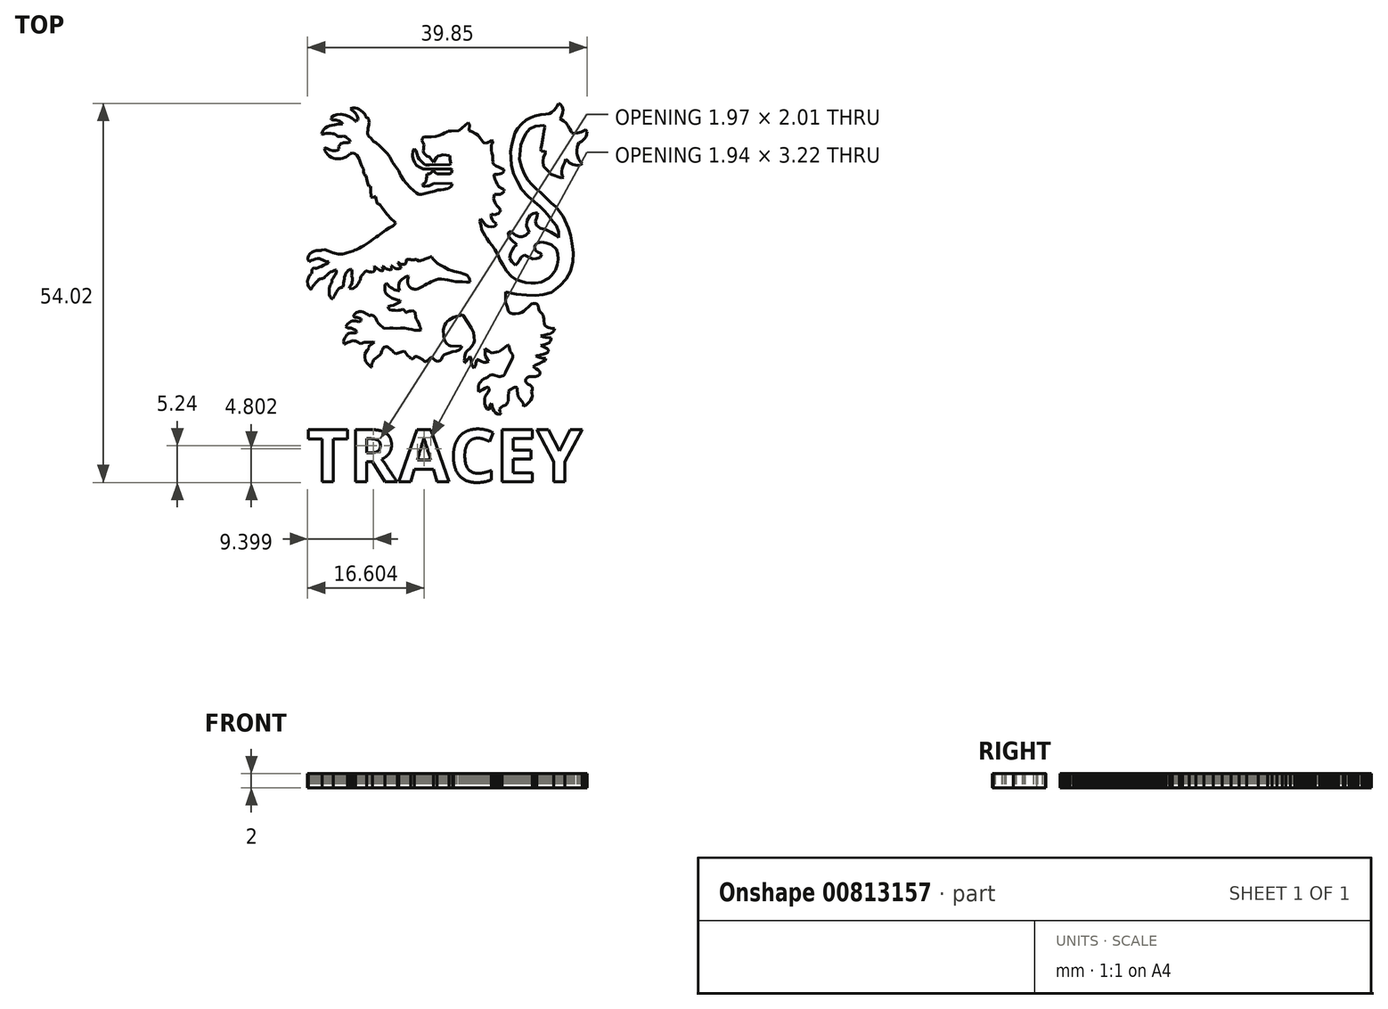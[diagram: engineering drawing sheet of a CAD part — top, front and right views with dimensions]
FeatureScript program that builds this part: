
annotation { "Feature Type Name" : "Feature", "Feature Type Description" : "" }
export const myFeature = defineFeature(function(context is Context, id is Id, definition is map)
    precondition{}
    {
        {
            var Q0;
            Q0=qCreatedBy(makeId("Top.planeOp"),FACE);
            var sketch = newSketch(context, id + "F0", { "sketchPlane" : qUnion([Q0])});
            skLineSegment(sketch, "E0", {"start": v(28.34, 17.71) * mm, "end": v(28.34, 16.2) * mm});
            skLineSegment(sketch, "E1", {"start": v(28.34, 16.2) * mm, "end": v(28.56, 15.55) * mm});
            skLineSegment(sketch, "E2", {"start": v(28.56, 15.55) * mm, "end": v(28.71, 15.03) * mm});
            skLineSegment(sketch, "E3", {"start": v(28.71, 15.03) * mm, "end": v(28.95, 14.75) * mm});
            skLineSegment(sketch, "E4", {"start": v(28.95, 14.75) * mm, "end": v(29.32, 14.64) * mm});
            skLineSegment(sketch, "E5", {"start": v(29.32, 14.64) * mm, "end": v(29.7, 14.64) * mm});
            skLineSegment(sketch, "E6", {"start": v(29.7, 14.64) * mm, "end": v(30.25, 14.7) * mm});
            skLineSegment(sketch, "E7", {"start": v(30.25, 14.7) * mm, "end": v(30.6, 14.84) * mm});
            skLineSegment(sketch, "E8", {"start": v(30.6, 14.84) * mm, "end": v(30.92, 15.03) * mm});
            skLineSegment(sketch, "E9", {"start": v(30.92, 15.03) * mm, "end": v(31.25, 15.3) * mm});
            skLineSegment(sketch, "E10", {"start": v(31.25, 15.3) * mm, "end": v(31.54, 15.57) * mm});
            skLineSegment(sketch, "E11", {"start": v(31.54, 15.57) * mm, "end": v(31.8, 15.85) * mm});
            skLineSegment(sketch, "E12", {"start": v(31.8, 15.85) * mm, "end": v(32.02, 16.03) * mm});
            skLineSegment(sketch, "E13", {"start": v(32.02, 16.03) * mm, "end": v(32.3, 16.1) * mm});
            skLineSegment(sketch, "E14", {"start": v(32.3, 16.1) * mm, "end": v(32.6, 16.1) * mm});
            skLineSegment(sketch, "E15", {"start": v(32.6, 16.1) * mm, "end": v(32.8, 16.04) * mm});
            skLineSegment(sketch, "E16", {"start": v(32.8, 16.04) * mm, "end": v(32.94, 15.82) * mm});
            skLineSegment(sketch, "E17", {"start": v(32.94, 15.82) * mm, "end": v(33.05, 15.36) * mm});
            skLineSegment(sketch, "E18", {"start": v(33.05, 15.36) * mm, "end": v(33.13, 15.03) * mm});
            skLineSegment(sketch, "E19", {"start": v(33.13, 15.03) * mm, "end": v(33.33, 14.83) * mm});
            skLineSegment(sketch, "E20", {"start": v(33.33, 14.83) * mm, "end": v(33.51, 14.64) * mm});
            skLineSegment(sketch, "E21", {"start": v(33.51, 14.64) * mm, "end": v(33.65, 14.4) * mm});
            skLineSegment(sketch, "E22", {"start": v(33.65, 14.4) * mm, "end": v(33.71, 14.17) * mm});
            skLineSegment(sketch, "E23", {"start": v(33.71, 14.17) * mm, "end": v(33.76, 13.87) * mm});
            skLineSegment(sketch, "E24", {"start": v(33.76, 13.87) * mm, "end": v(33.76, 13.58) * mm});
            skLineSegment(sketch, "E25", {"start": v(33.76, 13.58) * mm, "end": v(33.83, 13.25) * mm});
            skLineSegment(sketch, "E26", {"start": v(33.83, 13.25) * mm, "end": v(33.93, 12.98) * mm});
            skLineSegment(sketch, "E27", {"start": v(33.93, 12.98) * mm, "end": v(34.15, 12.8) * mm});
            skLineSegment(sketch, "E28", {"start": v(34.15, 12.8) * mm, "end": v(34.43, 12.66) * mm});
            skLineSegment(sketch, "E29", {"start": v(34.43, 12.66) * mm, "end": v(34.7, 12.58) * mm});
            skLineSegment(sketch, "E30", {"start": v(34.7, 12.58) * mm, "end": v(34.98, 12.5) * mm});
            skLineSegment(sketch, "E31", {"start": v(34.98, 12.5) * mm, "end": v(35.33, 12.5) * mm});
            skLineSegment(sketch, "E32", {"start": v(35.33, 12.5) * mm, "end": v(35.27, 12.3) * mm});
            skLineSegment(sketch, "E33", {"start": v(35.27, 12.3) * mm, "end": v(35.09, 12) * mm});
            skLineSegment(sketch, "E34", {"start": v(35.09, 12) * mm, "end": v(34.7, 11.8) * mm});
            skLineSegment(sketch, "E35", {"start": v(34.7, 11.8) * mm, "end": v(34.29, 11.7) * mm});
            skPoint(sketch, "E35.endSnap0", {"position": v(34.29, 12.73) * mm});
            skLineSegment(sketch, "E36", {"start": v(34.29, 11.7) * mm, "end": v(33.84, 11.57) * mm});
            skLineSegment(sketch, "E37", {"start": v(33.84, 11.57) * mm, "end": v(33.46, 11.52) * mm});
            skLineSegment(sketch, "E38", {"start": v(33.46, 11.52) * mm, "end": v(33.33, 11.44) * mm});
            skLineSegment(sketch, "E39", {"start": v(33.33, 11.44) * mm, "end": v(33.73, 11.33) * mm});
            skLineSegment(sketch, "E40", {"start": v(33.73, 11.33) * mm, "end": v(34.07, 11.28) * mm});
            skLineSegment(sketch, "E41", {"start": v(34.07, 11.28) * mm, "end": v(34.56, 11.22) * mm});
            skLineSegment(sketch, "E42", {"start": v(34.56, 11.22) * mm, "end": v(34.78, 11.22) * mm});
            skLineSegment(sketch, "E43", {"start": v(34.78, 11.22) * mm, "end": v(34.81, 10.91) * mm});
            skLineSegment(sketch, "E44", {"start": v(34.81, 10.91) * mm, "end": v(34.7, 10.7) * mm});
            skLineSegment(sketch, "E45", {"start": v(34.7, 10.7) * mm, "end": v(34.52, 10.52) * mm});
            skLineSegment(sketch, "E46", {"start": v(34.52, 10.52) * mm, "end": v(34.22, 10.35) * mm});
            skLineSegment(sketch, "E47", {"start": v(34.22, 10.35) * mm, "end": v(33.93, 10.26) * mm});
            skLineSegment(sketch, "E48", {"start": v(33.93, 10.26) * mm, "end": v(33.64, 10.19) * mm});
            skLineSegment(sketch, "E49", {"start": v(33.64, 10.19) * mm, "end": v(33.35, 10.14) * mm});
            skLineSegment(sketch, "E50", {"start": v(33.35, 10.14) * mm, "end": v(33.36, 10.09) * mm});
            skLineSegment(sketch, "E51", {"start": v(33.36, 10.09) * mm, "end": v(33.72, 9.9) * mm});
            skLineSegment(sketch, "E52", {"start": v(33.72, 9.9) * mm, "end": v(33.99, 9.77) * mm});
            skLineSegment(sketch, "E53", {"start": v(33.99, 9.77) * mm, "end": v(34.23, 9.64) * mm});
            skLineSegment(sketch, "E54", {"start": v(34.23, 9.64) * mm, "end": v(34.43, 9.48) * mm});
            skLineSegment(sketch, "E55", {"start": v(34.43, 9.48) * mm, "end": v(34.43, 9.29) * mm});
            skLineSegment(sketch, "E56", {"start": v(34.43, 9.29) * mm, "end": v(34.3, 9.12) * mm});
            skLineSegment(sketch, "E57", {"start": v(34.3, 9.12) * mm, "end": v(34.01, 8.96) * mm});
            skLineSegment(sketch, "E58", {"start": v(34.01, 8.96) * mm, "end": v(33.68, 8.84) * mm});
            skLineSegment(sketch, "E59", {"start": v(33.68, 8.84) * mm, "end": v(33.36, 8.75) * mm});
            skLineSegment(sketch, "E60", {"start": v(33.36, 8.75) * mm, "end": v(33.04, 8.68) * mm});
            skLineSegment(sketch, "E61", {"start": v(33.04, 8.68) * mm, "end": v(32.74, 8.62) * mm});
            skLineSegment(sketch, "E62", {"start": v(32.74, 8.62) * mm, "end": v(32.64, 8.59) * mm});
            skLineSegment(sketch, "E63", {"start": v(32.64, 8.59) * mm, "end": v(32.97, 8.49) * mm});
            skLineSegment(sketch, "E64", {"start": v(32.97, 8.49) * mm, "end": v(33.15, 8.4) * mm});
            skLineSegment(sketch, "E65", {"start": v(33.15, 8.4) * mm, "end": v(33.42, 8.31) * mm});
            skLineSegment(sketch, "E66", {"start": v(33.42, 8.31) * mm, "end": v(33.66, 8.29) * mm});
            skLineSegment(sketch, "E67", {"start": v(33.66, 8.29) * mm, "end": v(33.93, 8.29) * mm});
            skLineSegment(sketch, "E68", {"start": v(33.93, 8.29) * mm, "end": v(34.01, 8.26) * mm});
            skLineSegment(sketch, "E69", {"start": v(34.01, 8.26) * mm, "end": v(33.99, 7.95) * mm});
            skLineSegment(sketch, "E70", {"start": v(33.99, 7.95) * mm, "end": v(33.56, 7.73) * mm});
            skLineSegment(sketch, "E71", {"start": v(33.56, 7.73) * mm, "end": v(33.11, 7.52) * mm});
            skLineSegment(sketch, "E72", {"start": v(33.11, 7.52) * mm, "end": v(32.6, 7.32) * mm});
            skLineSegment(sketch, "E73", {"start": v(32.6, 7.32) * mm, "end": v(32.31, 7.16) * mm});
            skLineSegment(sketch, "E74", {"start": v(32.31, 7.16) * mm, "end": v(32.24, 7.09) * mm});
            skLineSegment(sketch, "E75", {"start": v(32.24, 7.09) * mm, "end": v(32.66, 6.84) * mm});
            skLineSegment(sketch, "E76", {"start": v(32.66, 6.84) * mm, "end": v(32.94, 6.63) * mm});
            skLineSegment(sketch, "E77", {"start": v(32.94, 6.63) * mm, "end": v(33.14, 6.43) * mm});
            skLineSegment(sketch, "E78", {"start": v(33.14, 6.43) * mm, "end": v(33.23, 6.27) * mm});
            skLineSegment(sketch, "E79", {"start": v(33.23, 6.27) * mm, "end": v(33.23, 5.99) * mm});
            skLineSegment(sketch, "E80", {"start": v(33.23, 5.99) * mm, "end": v(32.97, 5.78) * mm});
            skLineSegment(sketch, "E81", {"start": v(32.97, 5.78) * mm, "end": v(32.6, 5.7) * mm});
            skLineSegment(sketch, "E82", {"start": v(32.6, 5.7) * mm, "end": v(32.13, 5.7) * mm});
            skLineSegment(sketch, "E83", {"start": v(32.13, 5.7) * mm, "end": v(31.71, 5.7) * mm});
            skLineSegment(sketch, "E84", {"start": v(31.71, 5.7) * mm, "end": v(31.42, 5.56) * mm});
            skLineSegment(sketch, "E85", {"start": v(31.42, 5.56) * mm, "end": v(31.25, 5.36) * mm});
            skLineSegment(sketch, "E86", {"start": v(31.25, 5.36) * mm, "end": v(31.2, 5.21) * mm});
            skLineSegment(sketch, "E87", {"start": v(31.2, 5.21) * mm, "end": v(31.2, 5.07) * mm});
            skLineSegment(sketch, "E88", {"start": v(31.2, 5.07) * mm, "end": v(31.22, 4.95) * mm});
            skLineSegment(sketch, "E89", {"start": v(31.22, 4.95) * mm, "end": v(31.27, 4.82) * mm});
            skLineSegment(sketch, "E90", {"start": v(31.27, 4.82) * mm, "end": v(31.37, 4.69) * mm});
            skLineSegment(sketch, "E91", {"start": v(31.37, 4.69) * mm, "end": v(31.5, 4.61) * mm});
            skLineSegment(sketch, "E92", {"start": v(31.5, 4.61) * mm, "end": v(31.63, 4.52) * mm});
            skLineSegment(sketch, "E93", {"start": v(31.63, 4.52) * mm, "end": v(31.8, 4.44) * mm});
            skLineSegment(sketch, "E94", {"start": v(31.8, 4.44) * mm, "end": v(31.95, 4.33) * mm});
            skLineSegment(sketch, "E95", {"start": v(31.95, 4.33) * mm, "end": v(32.08, 4.2) * mm});
            skLineSegment(sketch, "E96", {"start": v(32.08, 4.2) * mm, "end": v(32.15, 4.06) * mm});
            skLineSegment(sketch, "E97", {"start": v(32.15, 4.06) * mm, "end": v(32.13, 3.81) * mm});
            skLineSegment(sketch, "E98", {"start": v(32.13, 3.81) * mm, "end": v(32.05, 3.64) * mm});
            skLineSegment(sketch, "E99", {"start": v(32.05, 3.64) * mm, "end": v(31.98, 3.52) * mm});
            skLineSegment(sketch, "E100", {"start": v(31.98, 3.52) * mm, "end": v(32.06, 3.31) * mm});
            skLineSegment(sketch, "E101", {"start": v(32.06, 3.31) * mm, "end": v(32.1, 3.15) * mm});
            skLineSegment(sketch, "E102", {"start": v(32.1, 3.15) * mm, "end": v(32.15, 2.91) * mm});
            skLineSegment(sketch, "E103", {"start": v(32.15, 2.91) * mm, "end": v(32.05, 2.6) * mm});
            skLineSegment(sketch, "E104", {"start": v(32.05, 2.6) * mm, "end": v(31.9, 2.32) * mm});
            skLineSegment(sketch, "E105", {"start": v(31.9, 2.32) * mm, "end": v(31.75, 2.1) * mm});
            skLineSegment(sketch, "E106", {"start": v(31.75, 2.1) * mm, "end": v(31.46, 1.82) * mm});
            skLineSegment(sketch, "E107", {"start": v(31.46, 1.82) * mm, "end": v(31.25, 1.61) * mm});
            skLineSegment(sketch, "E108", {"start": v(31.25, 1.61) * mm, "end": v(30.95, 1.48) * mm});
            skLineSegment(sketch, "E109", {"start": v(30.95, 1.48) * mm, "end": v(30.85, 1.43) * mm});
            skLineSegment(sketch, "E110", {"start": v(30.85, 1.43) * mm, "end": v(30.9, 1.83) * mm});
            skLineSegment(sketch, "E111", {"start": v(30.9, 1.83) * mm, "end": v(30.64, 2.2) * mm});
            skLineSegment(sketch, "E112", {"start": v(30.64, 2.2) * mm, "end": v(30.14, 2.84) * mm});
            skLineSegment(sketch, "E113", {"start": v(30.14, 2.84) * mm, "end": v(30.04, 3.24) * mm});
            skLineSegment(sketch, "E114", {"start": v(30.04, 3.24) * mm, "end": v(29.97, 3.72) * mm});
            skLineSegment(sketch, "E115", {"start": v(29.97, 3.72) * mm, "end": v(29.97, 4.06) * mm});
            skLineSegment(sketch, "E116", {"start": v(29.97, 4.06) * mm, "end": v(29.84, 4.15) * mm});
            skLineSegment(sketch, "E117", {"start": v(29.84, 4.15) * mm, "end": v(29.57, 4.11) * mm});
            skLineSegment(sketch, "E118", {"start": v(29.57, 4.11) * mm, "end": v(29.25, 3.93) * mm});
            skLineSegment(sketch, "E119", {"start": v(29.25, 3.93) * mm, "end": v(28.9, 3.74) * mm});
            skLineSegment(sketch, "E120", {"start": v(28.9, 3.74) * mm, "end": v(28.71, 3.56) * mm});
            skLineSegment(sketch, "E121", {"start": v(28.71, 3.56) * mm, "end": v(28.74, 3.42) * mm});
            skLineSegment(sketch, "E122", {"start": v(28.74, 3.42) * mm, "end": v(28.71, 2.94) * mm});
            skLineSegment(sketch, "E123", {"start": v(28.71, 2.94) * mm, "end": v(28.71, 2.18) * mm});
            skLineSegment(sketch, "E124", {"start": v(28.71, 2.18) * mm, "end": v(28.6, 1.96) * mm});
            skLineSegment(sketch, "E125", {"start": v(28.6, 1.96) * mm, "end": v(28.55, 1.77) * mm});
            skLineSegment(sketch, "E126", {"start": v(28.55, 1.77) * mm, "end": v(28.34, 1.58) * mm});
            skLineSegment(sketch, "E127", {"start": v(28.34, 1.58) * mm, "end": v(27.92, 1.48) * mm});
            skLineSegment(sketch, "E128", {"start": v(27.92, 1.48) * mm, "end": v(27.7, 1.3) * mm});
            skLineSegment(sketch, "E129", {"start": v(27.7, 1.3) * mm, "end": v(27.45, 1.02) * mm});
            skLineSegment(sketch, "E130", {"start": v(27.45, 1.02) * mm, "end": v(27.51, 0.72) * mm});
            skLineSegment(sketch, "E131", {"start": v(27.51, 0.72) * mm, "end": v(27.62, 0.54) * mm});
            skLineSegment(sketch, "E132", {"start": v(27.62, 0.54) * mm, "end": v(27.56, 0.35) * mm});
            skLineSegment(sketch, "E133", {"start": v(27.56, 0.35) * mm, "end": v(27.35, 0.24) * mm});
            skLineSegment(sketch, "E134", {"start": v(27.35, 0.24) * mm, "end": v(27.18, 0.32) * mm});
            skLineSegment(sketch, "E135", {"start": v(27.18, 0.32) * mm, "end": v(26.9, 0.53) * mm});
            skLineSegment(sketch, "E136", {"start": v(26.9, 0.53) * mm, "end": v(26.68, 0.8) * mm});
            skLineSegment(sketch, "E137", {"start": v(26.68, 0.8) * mm, "end": v(26.47, 1.12) * mm});
            skLineSegment(sketch, "E138", {"start": v(26.47, 1.12) * mm, "end": v(26.41, 1.5) * mm});
            skLineSegment(sketch, "E139", {"start": v(26.41, 1.5) * mm, "end": v(26.37, 1.76) * mm});
            skLineSegment(sketch, "E140", {"start": v(26.37, 1.76) * mm, "end": v(26.32, 1.84) * mm});
            skLineSegment(sketch, "E141", {"start": v(26.32, 1.84) * mm, "end": v(26.2, 1.7) * mm});
            skLineSegment(sketch, "E142", {"start": v(26.2, 1.7) * mm, "end": v(26.12, 1.47) * mm});
            skLineSegment(sketch, "E143", {"start": v(26.12, 1.47) * mm, "end": v(26.07, 1.3) * mm});
            skLineSegment(sketch, "E144", {"start": v(26.07, 1.3) * mm, "end": v(26.07, 1.14) * mm});
            skLineSegment(sketch, "E145", {"start": v(26.07, 1.14) * mm, "end": v(26.07, 0.96) * mm});
            skLineSegment(sketch, "E146", {"start": v(26.07, 0.96) * mm, "end": v(25.73, 1.02) * mm});
            skLineSegment(sketch, "E147", {"start": v(25.73, 1.02) * mm, "end": v(25.4, 1.53) * mm});
            skLineSegment(sketch, "E148", {"start": v(25.4, 1.53) * mm, "end": v(25.32, 1.85) * mm});
            skLineSegment(sketch, "E149", {"start": v(25.32, 1.85) * mm, "end": v(25.32, 2.5) * mm});
            skLineSegment(sketch, "E150", {"start": v(25.32, 2.5) * mm, "end": v(25.43, 2.86) * mm});
            skLineSegment(sketch, "E151", {"start": v(25.43, 2.86) * mm, "end": v(25.64, 3.16) * mm});
            skLineSegment(sketch, "E152", {"start": v(25.64, 3.16) * mm, "end": v(25.85, 3.44) * mm});
            skLineSegment(sketch, "E153", {"start": v(25.85, 3.44) * mm, "end": v(26, 3.74) * mm});
            skLineSegment(sketch, "E154", {"start": v(26, 3.74) * mm, "end": v(26, 3.97) * mm});
            skLineSegment(sketch, "E155", {"start": v(26, 3.97) * mm, "end": v(25.84, 4.11) * mm});
            skLineSegment(sketch, "E156", {"start": v(25.84, 4.11) * mm, "end": v(25.68, 4.11) * mm});
            skLineSegment(sketch, "E157", {"start": v(25.68, 4.11) * mm, "end": v(25.43, 4.02) * mm});
            skLineSegment(sketch, "E158", {"start": v(25.43, 4.02) * mm, "end": v(25.09, 3.83) * mm});
            skLineSegment(sketch, "E159", {"start": v(25.09, 3.83) * mm, "end": v(24.86, 3.68) * mm});
            skLineSegment(sketch, "E160", {"start": v(24.86, 3.68) * mm, "end": v(24.55, 3.48) * mm});
            skLineSegment(sketch, "E161", {"start": v(24.55, 3.48) * mm, "end": v(24.48, 3.69) * mm});
            skLineSegment(sketch, "E162", {"start": v(24.48, 3.69) * mm, "end": v(24.48, 3.93) * mm});
            skLineSegment(sketch, "E163", {"start": v(24.48, 3.93) * mm, "end": v(24.48, 4.23) * mm});
            skLineSegment(sketch, "E164", {"start": v(24.48, 4.23) * mm, "end": v(24.55, 4.66) * mm});
            skLineSegment(sketch, "E165", {"start": v(24.55, 4.66) * mm, "end": v(24.74, 4.93) * mm});
            skLineSegment(sketch, "E166", {"start": v(24.74, 4.93) * mm, "end": v(24.96, 5.17) * mm});
            skLineSegment(sketch, "E167", {"start": v(24.96, 5.17) * mm, "end": v(25.24, 5.32) * mm});
            skLineSegment(sketch, "E168", {"start": v(25.24, 5.32) * mm, "end": v(25.55, 5.45) * mm});
            skLineSegment(sketch, "E169", {"start": v(25.55, 5.45) * mm, "end": v(25.69, 5.48) * mm});
            skLineSegment(sketch, "E170", {"start": v(25.69, 5.48) * mm, "end": v(25.91, 5.73) * mm});
            skLineSegment(sketch, "E171", {"start": v(25.91, 5.73) * mm, "end": v(26.12, 5.85) * mm});
            skLineSegment(sketch, "E172", {"start": v(26.12, 5.85) * mm, "end": v(26.35, 5.93) * mm});
            skLineSegment(sketch, "E173", {"start": v(26.35, 5.93) * mm, "end": v(26.54, 5.93) * mm});
            skLineSegment(sketch, "E174", {"start": v(26.54, 5.93) * mm, "end": v(26.78, 5.86) * mm});
            skLineSegment(sketch, "E175", {"start": v(26.78, 5.86) * mm, "end": v(27, 5.8) * mm});
            skLineSegment(sketch, "E176", {"start": v(27, 5.8) * mm, "end": v(27.15, 5.75) * mm});
            skLineSegment(sketch, "E177", {"start": v(27.15, 5.75) * mm, "end": v(27.38, 5.68) * mm});
            skLineSegment(sketch, "E178", {"start": v(27.38, 5.68) * mm, "end": v(27.58, 5.68) * mm});
            skLineSegment(sketch, "E179", {"start": v(27.58, 5.68) * mm, "end": v(27.78, 5.72) * mm});
            skLineSegment(sketch, "E180", {"start": v(27.78, 5.72) * mm, "end": v(28, 5.8) * mm});
            skLineSegment(sketch, "E181", {"start": v(28, 5.8) * mm, "end": v(28.13, 5.92) * mm});
            skLineSegment(sketch, "E182", {"start": v(28.13, 5.92) * mm, "end": v(28.27, 6.12) * mm});
            skLineSegment(sketch, "E183", {"start": v(28.27, 6.12) * mm, "end": v(28.34, 6.35) * mm});
            skLineSegment(sketch, "E184", {"start": v(28.34, 6.35) * mm, "end": v(29.3, 8.22) * mm});
            skLineSegment(sketch, "E185", {"start": v(29.3, 8.22) * mm, "end": v(29.36, 8.45) * mm});
            skLineSegment(sketch, "E186", {"start": v(29.36, 8.45) * mm, "end": v(29.32, 8.78) * mm});
            skLineSegment(sketch, "E187", {"start": v(29.32, 8.78) * mm, "end": v(29.1, 9.12) * mm});
            skLineSegment(sketch, "E188", {"start": v(29.1, 9.12) * mm, "end": v(28.97, 9.32) * mm});
            skLineSegment(sketch, "E189", {"start": v(28.97, 9.32) * mm, "end": v(28.9, 9.66) * mm});
            skLineSegment(sketch, "E190", {"start": v(28.9, 9.66) * mm, "end": v(28.82, 9.97) * mm});
            skLineSegment(sketch, "E191", {"start": v(28.82, 9.97) * mm, "end": v(28.78, 10.13) * mm});
            skLineSegment(sketch, "E192", {"start": v(28.78, 10.13) * mm, "end": v(28.67, 10.16) * mm});
            skLineSegment(sketch, "E193", {"start": v(28.67, 10.16) * mm, "end": v(28.53, 10.05) * mm});
            skLineSegment(sketch, "E194", {"start": v(28.53, 10.05) * mm, "end": v(28.24, 9.82) * mm});
            skLineSegment(sketch, "E195", {"start": v(28.24, 9.82) * mm, "end": v(28.04, 9.66) * mm});
            skLineSegment(sketch, "E196", {"start": v(28.04, 9.66) * mm, "end": v(27.74, 9.46) * mm});
            skLineSegment(sketch, "E197", {"start": v(27.74, 9.46) * mm, "end": v(27.35, 9.25) * mm});
            skLineSegment(sketch, "E198", {"start": v(27.35, 9.25) * mm, "end": v(27, 9.14) * mm});
            skLineSegment(sketch, "E199", {"start": v(27, 9.14) * mm, "end": v(26.37, 9.05) * mm});
            skLineSegment(sketch, "E200", {"start": v(26.37, 9.05) * mm, "end": v(25.9, 9.29) * mm});
            skLineSegment(sketch, "E201", {"start": v(25.9, 9.29) * mm, "end": v(25.43, 9.63) * mm});
            skLineSegment(sketch, "E202", {"start": v(25.43, 9.63) * mm, "end": v(25.34, 9.66) * mm});
            skLineSegment(sketch, "E203", {"start": v(25.34, 9.66) * mm, "end": v(25.4, 9.42) * mm});
            skLineSegment(sketch, "E204", {"start": v(25.4, 9.42) * mm, "end": v(25.4, 9.12) * mm});
            skLineSegment(sketch, "E205", {"start": v(25.4, 9.12) * mm, "end": v(25.43, 8.86) * mm});
            skLineSegment(sketch, "E206", {"start": v(25.43, 8.86) * mm, "end": v(25.5, 8.54) * mm});
            skLineSegment(sketch, "E207", {"start": v(25.5, 8.54) * mm, "end": v(25.7, 8.2) * mm});
            skLineSegment(sketch, "E208", {"start": v(25.7, 8.2) * mm, "end": v(25.9, 7.85) * mm});
            skLineSegment(sketch, "E209", {"start": v(25.9, 7.85) * mm, "end": v(25.55, 7.7) * mm});
            skLineSegment(sketch, "E210", {"start": v(25.55, 7.7) * mm, "end": v(25.24, 7.7) * mm});
            skLineSegment(sketch, "E211", {"start": v(25.24, 7.7) * mm, "end": v(24.92, 7.8) * mm});
            skLineSegment(sketch, "E212", {"start": v(24.92, 7.8) * mm, "end": v(24.57, 7.98) * mm});
            skLineSegment(sketch, "E213", {"start": v(24.57, 7.98) * mm, "end": v(24.37, 8.08) * mm});
            skLineSegment(sketch, "E214", {"start": v(24.37, 8.08) * mm, "end": v(24.2, 8.08) * mm});
            skLineSegment(sketch, "E215", {"start": v(24.2, 8.08) * mm, "end": v(24.2, 7.96) * mm});
            skLineSegment(sketch, "E216", {"start": v(24.2, 7.96) * mm, "end": v(24.12, 7.73) * mm});
            skLineSegment(sketch, "E217", {"start": v(24.12, 7.73) * mm, "end": v(24.07, 7.57) * mm});
            skLineSegment(sketch, "E218", {"start": v(24.07, 7.57) * mm, "end": v(24.05, 7.4) * mm});
            skLineSegment(sketch, "E219", {"start": v(24.05, 7.4) * mm, "end": v(24, 7.23) * mm});
            skLineSegment(sketch, "E220", {"start": v(24, 7.23) * mm, "end": v(23.96, 7.1) * mm});
            skLineSegment(sketch, "E221", {"start": v(23.96, 7.1) * mm, "end": v(23.84, 6.85) * mm});
            skLineSegment(sketch, "E222", {"start": v(23.84, 6.85) * mm, "end": v(23.57, 7.2) * mm});
            skLineSegment(sketch, "E223", {"start": v(23.57, 7.2) * mm, "end": v(23.46, 7.65) * mm});
            skLineSegment(sketch, "E224", {"start": v(23.46, 7.65) * mm, "end": v(23.39, 8.17) * mm});
            skLineSegment(sketch, "E225", {"start": v(23.39, 8.17) * mm, "end": v(23.31, 8.49) * mm});
            skLineSegment(sketch, "E226", {"start": v(23.31, 8.49) * mm, "end": v(23.22, 8.55) * mm});
            skLineSegment(sketch, "E227", {"start": v(23.22, 8.55) * mm, "end": v(23.17, 8.48) * mm});
            skLineSegment(sketch, "E228", {"start": v(23.17, 8.48) * mm, "end": v(23.05, 8.24) * mm});
            skLineSegment(sketch, "E229", {"start": v(23.05, 8.24) * mm, "end": v(22.87, 8.03) * mm});
            skLineSegment(sketch, "E230", {"start": v(22.87, 8.03) * mm, "end": v(22.7, 7.85) * mm});
            skLineSegment(sketch, "E231", {"start": v(22.7, 7.85) * mm, "end": v(22.58, 7.68) * mm});
            skLineSegment(sketch, "E232", {"start": v(22.58, 7.68) * mm, "end": v(22.52, 7.64) * mm});
            skLineSegment(sketch, "E233", {"start": v(22.52, 7.64) * mm, "end": v(22.46, 7.73) * mm});
            skLineSegment(sketch, "E234", {"start": v(22.46, 7.73) * mm, "end": v(22.45, 7.98) * mm});
            skLineSegment(sketch, "E235", {"start": v(22.45, 7.98) * mm, "end": v(22.48, 8.2) * mm});
            skLineSegment(sketch, "E236", {"start": v(22.48, 8.2) * mm, "end": v(22.5, 8.48) * mm});
            skLineSegment(sketch, "E237", {"start": v(22.5, 8.48) * mm, "end": v(22.56, 8.78) * mm});
            skLineSegment(sketch, "E238", {"start": v(22.56, 8.78) * mm, "end": v(22.67, 9.17) * mm});
            skLineSegment(sketch, "E239", {"start": v(22.67, 9.17) * mm, "end": v(22.94, 9.43) * mm});
            skLineSegment(sketch, "E240", {"start": v(22.94, 9.43) * mm, "end": v(23.18, 9.62) * mm});
            skLineSegment(sketch, "E241", {"start": v(23.18, 9.62) * mm, "end": v(23.53, 9.96) * mm});
            skLineSegment(sketch, "E242", {"start": v(23.53, 9.96) * mm, "end": v(23.74, 10.37) * mm});
            skLineSegment(sketch, "E243", {"start": v(23.74, 10.37) * mm, "end": v(23.86, 10.76) * mm});
            skLineSegment(sketch, "E244", {"start": v(23.86, 10.76) * mm, "end": v(23.84, 11.37) * mm});
            skLineSegment(sketch, "E245", {"start": v(23.84, 11.37) * mm, "end": v(23.76, 11.94) * mm});
            skLineSegment(sketch, "E246", {"start": v(23.76, 11.94) * mm, "end": v(23.43, 12.62) * mm});
            skLineSegment(sketch, "E247", {"start": v(23.43, 12.62) * mm, "end": v(22.96, 13.35) * mm});
            skLineSegment(sketch, "E248", {"start": v(22.96, 13.35) * mm, "end": v(22.53, 14) * mm});
            skLineSegment(sketch, "E249", {"start": v(22.53, 14) * mm, "end": v(22.3, 14.37) * mm});
            skLineSegment(sketch, "E250", {"start": v(22.3, 14.37) * mm, "end": v(22.14, 14.48) * mm});
            skLineSegment(sketch, "E251", {"start": v(22.14, 14.48) * mm, "end": v(21.82, 14.37) * mm});
            skLineSegment(sketch, "E252", {"start": v(21.82, 14.37) * mm, "end": v(21.28, 14.24) * mm});
            skLineSegment(sketch, "E253", {"start": v(21.28, 14.24) * mm, "end": v(20.87, 14.1) * mm});
            skLineSegment(sketch, "E254", {"start": v(20.87, 14.1) * mm, "end": v(20.56, 13.94) * mm});
            skLineSegment(sketch, "E255", {"start": v(20.56, 13.94) * mm, "end": v(20.26, 13.7) * mm});
            skLineSegment(sketch, "E256", {"start": v(20.26, 13.7) * mm, "end": v(20.02, 13.54) * mm});
            skLineSegment(sketch, "E257", {"start": v(20.02, 13.54) * mm, "end": v(19.8, 13.3) * mm});
            skLineSegment(sketch, "E258", {"start": v(19.8, 13.3) * mm, "end": v(19.63, 12.98) * mm});
            skLineSegment(sketch, "E259", {"start": v(19.63, 12.98) * mm, "end": v(19.54, 12.66) * mm});
            skLineSegment(sketch, "E260", {"start": v(19.54, 12.66) * mm, "end": v(19.45, 12.35) * mm});
            skLineSegment(sketch, "E261", {"start": v(19.45, 12.35) * mm, "end": v(19.46, 11.9) * mm});
            skLineSegment(sketch, "E262", {"start": v(19.46, 11.9) * mm, "end": v(19.48, 11.42) * mm});
            skLineSegment(sketch, "E263", {"start": v(19.48, 11.42) * mm, "end": v(19.57, 11) * mm});
            skLineSegment(sketch, "E264", {"start": v(19.57, 11) * mm, "end": v(19.7, 10.67) * mm});
            skLineSegment(sketch, "E265", {"start": v(19.7, 10.67) * mm, "end": v(19.93, 10.39) * mm});
            skLineSegment(sketch, "E266", {"start": v(19.93, 10.39) * mm, "end": v(20.28, 10.14) * mm});
            skLineSegment(sketch, "E267", {"start": v(20.28, 10.14) * mm, "end": v(20.45, 10.05) * mm});
            skLineSegment(sketch, "E268", {"start": v(20.45, 10.05) * mm, "end": v(22.01, 10) * mm});
            skLineSegment(sketch, "E269", {"start": v(22.01, 10) * mm, "end": v(22.02, 9.77) * mm});
            skLineSegment(sketch, "E270", {"start": v(22.02, 9.77) * mm, "end": v(21.7, 9.48) * mm});
            skLineSegment(sketch, "E271", {"start": v(21.7, 9.48) * mm, "end": v(21.3, 9.29) * mm});
            skLineSegment(sketch, "E272", {"start": v(21.3, 9.29) * mm, "end": v(20.8, 9.22) * mm});
            skLineSegment(sketch, "E273", {"start": v(20.8, 9.22) * mm, "end": v(20.28, 9.06) * mm});
            skLineSegment(sketch, "E274", {"start": v(20.28, 9.06) * mm, "end": v(19.9, 8.92) * mm});
            skLineSegment(sketch, "E275", {"start": v(19.9, 8.92) * mm, "end": v(19.58, 8.79) * mm});
            skLineSegment(sketch, "E276", {"start": v(19.58, 8.79) * mm, "end": v(19.37, 8.56) * mm});
            skLineSegment(sketch, "E277", {"start": v(19.37, 8.56) * mm, "end": v(19.25, 8.35) * mm});
            skLineSegment(sketch, "E278", {"start": v(19.25, 8.35) * mm, "end": v(19.17, 8.15) * mm});
            skLineSegment(sketch, "E279", {"start": v(19.17, 8.15) * mm, "end": v(19.02, 7.98) * mm});
            skLineSegment(sketch, "E280", {"start": v(19.02, 7.98) * mm, "end": v(18.78, 7.9) * mm});
            skLineSegment(sketch, "E281", {"start": v(18.78, 7.9) * mm, "end": v(18.6, 7.85) * mm});
            skLineSegment(sketch, "E282", {"start": v(18.6, 7.85) * mm, "end": v(18.36, 7.93) * mm});
            skLineSegment(sketch, "E283", {"start": v(18.36, 7.93) * mm, "end": v(18.22, 8.03) * mm});
            skLineSegment(sketch, "E284", {"start": v(18.22, 8.03) * mm, "end": v(18.04, 8.18) * mm});
            skLineSegment(sketch, "E285", {"start": v(18.04, 8.18) * mm, "end": v(17.92, 8.29) * mm});
            skLineSegment(sketch, "E286", {"start": v(17.92, 8.29) * mm, "end": v(17.83, 8.4) * mm});
            skLineSegment(sketch, "E287", {"start": v(17.83, 8.4) * mm, "end": v(17.69, 8.4) * mm});
            skLineSegment(sketch, "E288", {"start": v(17.69, 8.4) * mm, "end": v(17.58, 8.33) * mm});
            skLineSegment(sketch, "E289", {"start": v(17.58, 8.33) * mm, "end": v(17.46, 8.22) * mm});
            skLineSegment(sketch, "E290", {"start": v(17.46, 8.22) * mm, "end": v(17.33, 8.08) * mm});
            skLineSegment(sketch, "E291", {"start": v(17.33, 8.08) * mm, "end": v(17.22, 7.98) * mm});
            skLineSegment(sketch, "E292", {"start": v(17.22, 7.98) * mm, "end": v(17.1, 7.87) * mm});
            skLineSegment(sketch, "E293", {"start": v(17.1, 7.87) * mm, "end": v(16.95, 7.77) * mm});
            skLineSegment(sketch, "E294", {"start": v(16.95, 7.77) * mm, "end": v(16.74, 7.9) * mm});
            skLineSegment(sketch, "E295", {"start": v(16.74, 7.9) * mm, "end": v(16.5, 8.1) * mm});
            skLineSegment(sketch, "E296", {"start": v(16.5, 8.1) * mm, "end": v(16.04, 8.35) * mm});
            skLineSegment(sketch, "E297", {"start": v(16.04, 8.35) * mm, "end": v(15.82, 8.48) * mm});
            skLineSegment(sketch, "E298", {"start": v(15.82, 8.48) * mm, "end": v(15.74, 8.52) * mm});
            skLineSegment(sketch, "E299", {"start": v(15.74, 8.52) * mm, "end": v(15.67, 8.55) * mm});
            skLineSegment(sketch, "E300", {"start": v(15.67, 8.55) * mm, "end": v(15.55, 8.54) * mm});
            skLineSegment(sketch, "E301", {"start": v(15.55, 8.54) * mm, "end": v(15.39, 8.54) * mm});
            skLineSegment(sketch, "E302", {"start": v(15.39, 8.54) * mm, "end": v(15.34, 8.45) * mm});
            skLineSegment(sketch, "E303", {"start": v(15.34, 8.45) * mm, "end": v(15.26, 8.32) * mm});
            skLineSegment(sketch, "E304", {"start": v(15.26, 8.32) * mm, "end": v(15.14, 8.23) * mm});
            skLineSegment(sketch, "E305", {"start": v(15.14, 8.23) * mm, "end": v(15, 8.18) * mm});
            skLineSegment(sketch, "E306", {"start": v(15, 8.18) * mm, "end": v(14.88, 8.23) * mm});
            skLineSegment(sketch, "E307", {"start": v(14.88, 8.23) * mm, "end": v(14.78, 8.33) * mm});
            skLineSegment(sketch, "E308", {"start": v(14.78, 8.33) * mm, "end": v(14.64, 8.43) * mm});
            skLineSegment(sketch, "E309", {"start": v(14.64, 8.43) * mm, "end": v(14.56, 8.54) * mm});
            skLineSegment(sketch, "E310", {"start": v(14.56, 8.54) * mm, "end": v(14.36, 8.65) * mm});
            skLineSegment(sketch, "E311", {"start": v(14.36, 8.65) * mm, "end": v(14.25, 8.79) * mm});
            skLineSegment(sketch, "E312", {"start": v(14.25, 8.79) * mm, "end": v(14.12, 8.96) * mm});
            skLineSegment(sketch, "E313", {"start": v(14.12, 8.96) * mm, "end": v(14, 9.13) * mm});
            skLineSegment(sketch, "E314", {"start": v(14, 9.13) * mm, "end": v(13.9, 9.26) * mm});
            skLineSegment(sketch, "E315", {"start": v(13.9, 9.26) * mm, "end": v(13.6, 9.24) * mm});
            skLineSegment(sketch, "E316", {"start": v(13.6, 9.24) * mm, "end": v(13.22, 9.11) * mm});
            skLineSegment(sketch, "E317", {"start": v(13.22, 9.11) * mm, "end": v(13, 9.01) * mm});
            skLineSegment(sketch, "E318", {"start": v(13, 9.01) * mm, "end": v(12.82, 8.95) * mm});
            skLineSegment(sketch, "E319", {"start": v(12.82, 8.95) * mm, "end": v(12.67, 8.9) * mm});
            skLineSegment(sketch, "E320", {"start": v(12.67, 8.9) * mm, "end": v(12.49, 9) * mm});
            skLineSegment(sketch, "E321", {"start": v(12.49, 9) * mm, "end": v(12.36, 9.13) * mm});
            skLineSegment(sketch, "E322", {"start": v(12.36, 9.13) * mm, "end": v(12.2, 9.36) * mm});
            skLineSegment(sketch, "E323", {"start": v(12.2, 9.36) * mm, "end": v(11.93, 9.53) * mm});
            skLineSegment(sketch, "E324", {"start": v(11.93, 9.53) * mm, "end": v(11.58, 9.84) * mm});
            skLineSegment(sketch, "E325", {"start": v(11.58, 9.84) * mm, "end": v(11.42, 9.93) * mm});
            skLineSegment(sketch, "E326", {"start": v(11.42, 9.93) * mm, "end": v(11.23, 9.93) * mm});
            skLineSegment(sketch, "E327", {"start": v(11.23, 9.93) * mm, "end": v(11.02, 9.88) * mm});
            skLineSegment(sketch, "E328", {"start": v(11.02, 9.88) * mm, "end": v(10.89, 9.73) * mm});
            skLineSegment(sketch, "E329", {"start": v(10.89, 9.73) * mm, "end": v(10.78, 9.55) * mm});
            skLineSegment(sketch, "E330", {"start": v(10.78, 9.55) * mm, "end": v(10.67, 9.34) * mm});
            skLineSegment(sketch, "E331", {"start": v(10.67, 9.34) * mm, "end": v(10.53, 8.93) * mm});
            skLineSegment(sketch, "E332", {"start": v(10.53, 8.93) * mm, "end": v(10.45, 8.79) * mm});
            skLineSegment(sketch, "E333", {"start": v(10.45, 8.79) * mm, "end": v(10.24, 8.64) * mm});
            skLineSegment(sketch, "E334", {"start": v(10.24, 8.64) * mm, "end": v(10.02, 8.47) * mm});
            skLineSegment(sketch, "E335", {"start": v(10.02, 8.47) * mm, "end": v(9.78, 8.28) * mm});
            skLineSegment(sketch, "E336", {"start": v(9.78, 8.28) * mm, "end": v(9.56, 8.08) * mm});
            skLineSegment(sketch, "E337", {"start": v(9.56, 8.08) * mm, "end": v(9.48, 7.93) * mm});
            skLineSegment(sketch, "E338", {"start": v(9.48, 7.93) * mm, "end": v(9.4, 7.74) * mm});
            skLineSegment(sketch, "E339", {"start": v(9.4, 7.74) * mm, "end": v(9.3, 7.54) * mm});
            skLineSegment(sketch, "E340", {"start": v(9.3, 7.54) * mm, "end": v(9.22, 7.34) * mm});
            skLineSegment(sketch, "E341", {"start": v(9.22, 7.34) * mm, "end": v(9.2, 7.19) * mm});
            skLineSegment(sketch, "E342", {"start": v(9.2, 7.19) * mm, "end": v(9.2, 7) * mm});
            skLineSegment(sketch, "E343", {"start": v(9.2, 7) * mm, "end": v(9.13, 7) * mm});
            skLineSegment(sketch, "E344", {"start": v(9.13, 7) * mm, "end": v(8.79, 7.35) * mm});
            skLineSegment(sketch, "E345", {"start": v(8.79, 7.35) * mm, "end": v(8.6, 7.54) * mm});
            skLineSegment(sketch, "E346", {"start": v(8.6, 7.54) * mm, "end": v(8.42, 7.8) * mm});
            skLineSegment(sketch, "E347", {"start": v(8.42, 7.8) * mm, "end": v(8.32, 8.01) * mm});
            skLineSegment(sketch, "E348", {"start": v(8.32, 8.01) * mm, "end": v(8.3, 8.4) * mm});
            skLineSegment(sketch, "E349", {"start": v(8.3, 8.4) * mm, "end": v(8.3, 8.93) * mm});
            skLineSegment(sketch, "E350", {"start": v(8.3, 8.93) * mm, "end": v(8.43, 9.19) * mm});
            skLineSegment(sketch, "E351", {"start": v(8.43, 9.19) * mm, "end": v(8.55, 9.4) * mm});
            skLineSegment(sketch, "E352", {"start": v(8.55, 9.4) * mm, "end": v(8.7, 9.55) * mm});
            skLineSegment(sketch, "E353", {"start": v(8.7, 9.55) * mm, "end": v(8.81, 9.73) * mm});
            skLineSegment(sketch, "E354", {"start": v(8.81, 9.73) * mm, "end": v(8.77, 9.88) * mm});
            skLineSegment(sketch, "E355", {"start": v(8.77, 9.88) * mm, "end": v(8.87, 10.05) * mm});
            skLineSegment(sketch, "E356", {"start": v(8.87, 10.05) * mm, "end": v(9.06, 10.2) * mm});
            skLineSegment(sketch, "E357", {"start": v(9.06, 10.2) * mm, "end": v(9.26, 10.31) * mm});
            skLineSegment(sketch, "E358", {"start": v(9.26, 10.31) * mm, "end": v(9.47, 10.47) * mm});
            skLineSegment(sketch, "E359", {"start": v(9.47, 10.47) * mm, "end": v(9.57, 10.54) * mm});
            skLineSegment(sketch, "E360", {"start": v(9.57, 10.54) * mm, "end": v(9.52, 10.61) * mm});
            skLineSegment(sketch, "E361", {"start": v(9.52, 10.61) * mm, "end": v(9.2, 10.59) * mm});
            skLineSegment(sketch, "E362", {"start": v(9.2, 10.59) * mm, "end": v(8.78, 10.59) * mm});
            skLineSegment(sketch, "E363", {"start": v(8.78, 10.59) * mm, "end": v(8.42, 10.56) * mm});
            skLineSegment(sketch, "E364", {"start": v(8.42, 10.56) * mm, "end": v(8.2, 10.55) * mm});
            skLineSegment(sketch, "E365", {"start": v(8.2, 10.55) * mm, "end": v(7.92, 10.46) * mm});
            skLineSegment(sketch, "E366", {"start": v(7.92, 10.46) * mm, "end": v(7.68, 10.38) * mm});
            skLineSegment(sketch, "E367", {"start": v(7.68, 10.38) * mm, "end": v(7.48, 10.4) * mm});
            skLineSegment(sketch, "E368", {"start": v(7.48, 10.4) * mm, "end": v(7.29, 10.53) * mm});
            skLineSegment(sketch, "E369", {"start": v(7.29, 10.53) * mm, "end": v(6.93, 10.72) * mm});
            skLineSegment(sketch, "E370", {"start": v(6.93, 10.72) * mm, "end": v(6.71, 10.76) * mm});
            skLineSegment(sketch, "E371", {"start": v(6.71, 10.76) * mm, "end": v(6.53, 10.78) * mm});
            skLineSegment(sketch, "E372", {"start": v(6.53, 10.78) * mm, "end": v(6.33, 10.72) * mm});
            skLineSegment(sketch, "E373", {"start": v(6.33, 10.72) * mm, "end": v(6.09, 10.64) * mm});
            skLineSegment(sketch, "E374", {"start": v(6.09, 10.64) * mm, "end": v(5.87, 10.53) * mm});
            skLineSegment(sketch, "E375", {"start": v(5.87, 10.53) * mm, "end": v(5.6, 10.41) * mm});
            skLineSegment(sketch, "E376", {"start": v(5.6, 10.41) * mm, "end": v(5.49, 10.3) * mm});
            skLineSegment(sketch, "E377", {"start": v(5.49, 10.3) * mm, "end": v(5.37, 10.28) * mm});
            skLineSegment(sketch, "E378", {"start": v(5.37, 10.28) * mm, "end": v(5.2, 10.66) * mm});
            skLineSegment(sketch, "E379", {"start": v(5.2, 10.66) * mm, "end": v(5.3, 10.93) * mm});
            skLineSegment(sketch, "E380", {"start": v(5.3, 10.93) * mm, "end": v(5.39, 11.2) * mm});
            skLineSegment(sketch, "E381", {"start": v(5.39, 11.2) * mm, "end": v(5.59, 11.44) * mm});
            skLineSegment(sketch, "E382", {"start": v(5.59, 11.44) * mm, "end": v(5.73, 11.7) * mm});
            skLineSegment(sketch, "E383", {"start": v(5.73, 11.7) * mm, "end": v(5.96, 11.81) * mm});
            skLineSegment(sketch, "E384", {"start": v(5.96, 11.81) * mm, "end": v(6.27, 11.86) * mm});
            skLineSegment(sketch, "E385", {"start": v(6.27, 11.86) * mm, "end": v(6.58, 11.86) * mm});
            skLineSegment(sketch, "E386", {"start": v(6.58, 11.86) * mm, "end": v(6.85, 11.87) * mm});
            skLineSegment(sketch, "E387", {"start": v(6.85, 11.87) * mm, "end": v(7.03, 11.94) * mm});
            skLineSegment(sketch, "E388", {"start": v(7.03, 11.94) * mm, "end": v(7.1, 12.06) * mm});
            skLineSegment(sketch, "E389", {"start": v(7.1, 12.06) * mm, "end": v(6.86, 12.3) * mm});
            skLineSegment(sketch, "E390", {"start": v(6.86, 12.3) * mm, "end": v(6.67, 12.4) * mm});
            skLineSegment(sketch, "E391", {"start": v(6.67, 12.4) * mm, "end": v(6.44, 12.5) * mm});
            skLineSegment(sketch, "E392", {"start": v(6.44, 12.5) * mm, "end": v(6.27, 12.59) * mm});
            skLineSegment(sketch, "E393", {"start": v(6.27, 12.59) * mm, "end": v(6.04, 12.6) * mm});
            skLineSegment(sketch, "E394", {"start": v(6.04, 12.6) * mm, "end": v(5.76, 12.6) * mm});
            skLineSegment(sketch, "E395", {"start": v(5.76, 12.6) * mm, "end": v(5.6, 12.69) * mm});
            skLineSegment(sketch, "E396", {"start": v(5.6, 12.69) * mm, "end": v(5.54, 12.76) * mm});
            skLineSegment(sketch, "E397", {"start": v(5.54, 12.76) * mm, "end": v(5.67, 13) * mm});
            skLineSegment(sketch, "E398", {"start": v(5.67, 13) * mm, "end": v(5.77, 13.17) * mm});
            skLineSegment(sketch, "E399", {"start": v(5.77, 13.17) * mm, "end": v(5.93, 13.28) * mm});
            skLineSegment(sketch, "E400", {"start": v(5.93, 13.28) * mm, "end": v(6.1, 13.42) * mm});
            skLineSegment(sketch, "E401", {"start": v(6.1, 13.42) * mm, "end": v(6.33, 13.53) * mm});
            skLineSegment(sketch, "E402", {"start": v(6.33, 13.53) * mm, "end": v(6.5, 13.59) * mm});
            skLineSegment(sketch, "E403", {"start": v(6.5, 13.59) * mm, "end": v(6.68, 13.6) * mm});
            skLineSegment(sketch, "E404", {"start": v(6.68, 13.6) * mm, "end": v(6.97, 13.58) * mm});
            skLineSegment(sketch, "E405", {"start": v(6.97, 13.58) * mm, "end": v(7.2, 13.57) * mm});
            skLineSegment(sketch, "E406", {"start": v(7.2, 13.57) * mm, "end": v(7.39, 13.48) * mm});
            skLineSegment(sketch, "E407", {"start": v(7.39, 13.48) * mm, "end": v(7.66, 13.62) * mm});
            skLineSegment(sketch, "E408", {"start": v(7.66, 13.62) * mm, "end": v(7.73, 13.74) * mm});
            skLineSegment(sketch, "E409", {"start": v(7.73, 13.74) * mm, "end": v(7.72, 13.9) * mm});
            skLineSegment(sketch, "E410", {"start": v(7.72, 13.9) * mm, "end": v(7.52, 14.02) * mm});
            skLineSegment(sketch, "E411", {"start": v(7.52, 14.02) * mm, "end": v(7.33, 14.07) * mm});
            skLineSegment(sketch, "E412", {"start": v(7.33, 14.07) * mm, "end": v(7.1, 14.13) * mm});
            skLineSegment(sketch, "E413", {"start": v(7.1, 14.13) * mm, "end": v(6.88, 14.14) * mm});
            skLineSegment(sketch, "E414", {"start": v(6.88, 14.14) * mm, "end": v(6.73, 14.15) * mm});
            skLineSegment(sketch, "E415", {"start": v(6.73, 14.15) * mm, "end": v(6.68, 14.27) * mm});
            skLineSegment(sketch, "E416", {"start": v(6.68, 14.27) * mm, "end": v(6.67, 14.44) * mm});
            skLineSegment(sketch, "E417", {"start": v(6.67, 14.44) * mm, "end": v(6.84, 14.64) * mm});
            skLineSegment(sketch, "E418", {"start": v(6.84, 14.64) * mm, "end": v(7.05, 14.8) * mm});
            skLineSegment(sketch, "E419", {"start": v(7.05, 14.8) * mm, "end": v(7.29, 14.86) * mm});
            skLineSegment(sketch, "E420", {"start": v(7.29, 14.86) * mm, "end": v(7.46, 14.92) * mm});
            skLineSegment(sketch, "E421", {"start": v(7.46, 14.92) * mm, "end": v(7.73, 14.92) * mm});
            skLineSegment(sketch, "E422", {"start": v(7.73, 14.92) * mm, "end": v(8.02, 14.9) * mm});
            skLineSegment(sketch, "E423", {"start": v(8.02, 14.9) * mm, "end": v(8.3, 14.77) * mm});
            skLineSegment(sketch, "E424", {"start": v(8.3, 14.77) * mm, "end": v(8.45, 14.64) * mm});
            skLineSegment(sketch, "E425", {"start": v(8.45, 14.64) * mm, "end": v(8.62, 14.53) * mm});
            skLineSegment(sketch, "E426", {"start": v(8.62, 14.53) * mm, "end": v(8.74, 14.4) * mm});
            skLineSegment(sketch, "E427", {"start": v(8.74, 14.4) * mm, "end": v(8.8, 14.36) * mm});
            skLineSegment(sketch, "E428", {"start": v(8.8, 14.36) * mm, "end": v(8.96, 14.4) * mm});
            skLineSegment(sketch, "E429", {"start": v(8.96, 14.4) * mm, "end": v(9.09, 14.46) * mm});
            skLineSegment(sketch, "E430", {"start": v(9.09, 14.46) * mm, "end": v(9.24, 14.44) * mm});
            skLineSegment(sketch, "E431", {"start": v(9.24, 14.44) * mm, "end": v(9.4, 14.4) * mm});
            skLineSegment(sketch, "E432", {"start": v(9.4, 14.4) * mm, "end": v(9.55, 14.3) * mm});
            skLineSegment(sketch, "E433", {"start": v(9.55, 14.3) * mm, "end": v(9.66, 14.17) * mm});
            skLineSegment(sketch, "E434", {"start": v(9.66, 14.17) * mm, "end": v(9.76, 14.04) * mm});
            skLineSegment(sketch, "E435", {"start": v(9.76, 14.04) * mm, "end": v(9.84, 13.9) * mm});
            skLineSegment(sketch, "E436", {"start": v(9.84, 13.9) * mm, "end": v(9.92, 13.73) * mm});
            skLineSegment(sketch, "E437", {"start": v(9.92, 13.73) * mm, "end": v(9.98, 13.58) * mm});
            skLineSegment(sketch, "E438", {"start": v(9.98, 13.58) * mm, "end": v(10.05, 13.46) * mm});
            skLineSegment(sketch, "E439", {"start": v(10.05, 13.46) * mm, "end": v(10.18, 13.31) * mm});
            skLineSegment(sketch, "E440", {"start": v(10.18, 13.31) * mm, "end": v(10.3, 13.16) * mm});
            skLineSegment(sketch, "E441", {"start": v(10.3, 13.16) * mm, "end": v(10.45, 13.04) * mm});
            skLineSegment(sketch, "E442", {"start": v(10.45, 13.04) * mm, "end": v(10.58, 12.9) * mm});
            skLineSegment(sketch, "E443", {"start": v(10.58, 12.9) * mm, "end": v(10.73, 12.76) * mm});
            skLineSegment(sketch, "E444", {"start": v(10.73, 12.76) * mm, "end": v(10.87, 12.66) * mm});
            skLineSegment(sketch, "E445", {"start": v(10.87, 12.66) * mm, "end": v(10.98, 12.55) * mm});
            skLineSegment(sketch, "E446", {"start": v(10.98, 12.55) * mm, "end": v(11.02, 12.53) * mm});
            skLineSegment(sketch, "E447", {"start": v(11.02, 12.53) * mm, "end": v(11.84, 12.58) * mm});
            skLineSegment(sketch, "E448", {"start": v(11.84, 12.58) * mm, "end": v(12.28, 12.58) * mm});
            skLineSegment(sketch, "E449", {"start": v(12.28, 12.58) * mm, "end": v(12.76, 12.55) * mm});
            skLineSegment(sketch, "E450", {"start": v(12.76, 12.55) * mm, "end": v(13.36, 12.6) * mm});
            skLineSegment(sketch, "E451", {"start": v(13.36, 12.6) * mm, "end": v(13.94, 12.6) * mm});
            skLineSegment(sketch, "E452", {"start": v(13.94, 12.6) * mm, "end": v(14.47, 12.49) * mm});
            skLineSegment(sketch, "E453", {"start": v(14.47, 12.49) * mm, "end": v(14.9, 12.39) * mm});
            skLineSegment(sketch, "E454", {"start": v(14.9, 12.39) * mm, "end": v(15.4, 12.26) * mm});
            skLineSegment(sketch, "E455", {"start": v(15.4, 12.26) * mm, "end": v(15.65, 12.28) * mm});
            skLineSegment(sketch, "E456", {"start": v(15.65, 12.28) * mm, "end": v(16.17, 12.28) * mm});
            skLineSegment(sketch, "E457", {"start": v(16.17, 12.28) * mm, "end": v(16.24, 12.35) * mm});
            skLineSegment(sketch, "E458", {"start": v(16.24, 12.35) * mm, "end": v(16.22, 12.47) * mm});
            skLineSegment(sketch, "E459", {"start": v(16.22, 12.47) * mm, "end": v(16.21, 12.63) * mm});
            skLineSegment(sketch, "E460", {"start": v(16.21, 12.63) * mm, "end": v(16.1, 12.87) * mm});
            skLineSegment(sketch, "E461", {"start": v(16.1, 12.87) * mm, "end": v(15.93, 13.3) * mm});
            skLineSegment(sketch, "E462", {"start": v(15.93, 13.3) * mm, "end": v(15.68, 13.73) * mm});
            skLineSegment(sketch, "E463", {"start": v(15.68, 13.73) * mm, "end": v(15.57, 13.95) * mm});
            skLineSegment(sketch, "E464", {"start": v(15.57, 13.95) * mm, "end": v(15.5, 14.16) * mm});
            skLineSegment(sketch, "E465", {"start": v(15.5, 14.16) * mm, "end": v(15.48, 14.4) * mm});
            skLineSegment(sketch, "E466", {"start": v(15.48, 14.4) * mm, "end": v(15.45, 14.73) * mm});
            skLineSegment(sketch, "E467", {"start": v(15.45, 14.73) * mm, "end": v(15.35, 14.87) * mm});
            skLineSegment(sketch, "E468", {"start": v(15.35, 14.87) * mm, "end": v(15.19, 14.97) * mm});
            skLineSegment(sketch, "E469", {"start": v(15.19, 14.97) * mm, "end": v(15, 15.05) * mm});
            skLineSegment(sketch, "E470", {"start": v(15, 15.05) * mm, "end": v(14.82, 15.03) * mm});
            skLineSegment(sketch, "E471", {"start": v(14.82, 15.03) * mm, "end": v(14.61, 15) * mm});
            skLineSegment(sketch, "E472", {"start": v(14.61, 15) * mm, "end": v(14.45, 14.93) * mm});
            skLineSegment(sketch, "E473", {"start": v(14.45, 14.93) * mm, "end": v(14.3, 14.85) * mm});
            skLineSegment(sketch, "E474", {"start": v(14.3, 14.85) * mm, "end": v(14.21, 14.8) * mm});
            skLineSegment(sketch, "E475", {"start": v(14.21, 14.8) * mm, "end": v(14.08, 14.84) * mm});
            skLineSegment(sketch, "E476", {"start": v(14.08, 14.84) * mm, "end": v(13.92, 15.05) * mm});
            skLineSegment(sketch, "E477", {"start": v(13.92, 15.05) * mm, "end": v(13.77, 15.18) * mm});
            skLineSegment(sketch, "E478", {"start": v(13.77, 15.18) * mm, "end": v(13.66, 15.24) * mm});
            skLineSegment(sketch, "E479", {"start": v(13.66, 15.24) * mm, "end": v(13.46, 15.19) * mm});
            skLineSegment(sketch, "E480", {"start": v(13.46, 15.19) * mm, "end": v(13.27, 15.13) * mm});
            skLineSegment(sketch, "E481", {"start": v(13.27, 15.13) * mm, "end": v(13.09, 15.1) * mm});
            skLineSegment(sketch, "E482", {"start": v(13.09, 15.1) * mm, "end": v(12.83, 15.1) * mm});
            skLineSegment(sketch, "E483", {"start": v(12.83, 15.1) * mm, "end": v(12.52, 15.1) * mm});
            skLineSegment(sketch, "E484", {"start": v(12.52, 15.1) * mm, "end": v(12.13, 15.13) * mm});
            skLineSegment(sketch, "E485", {"start": v(12.13, 15.13) * mm, "end": v(11.83, 15.21) * mm});
            skLineSegment(sketch, "E486", {"start": v(11.83, 15.21) * mm, "end": v(11.67, 15.33) * mm});
            skLineSegment(sketch, "E487", {"start": v(11.67, 15.33) * mm, "end": v(11.56, 15.61) * mm});
            skLineSegment(sketch, "E488", {"start": v(11.56, 15.61) * mm, "end": v(11.73, 15.68) * mm});
            skLineSegment(sketch, "E489", {"start": v(11.73, 15.68) * mm, "end": v(11.96, 15.8) * mm});
            skLineSegment(sketch, "E490", {"start": v(11.96, 15.8) * mm, "end": v(12.3, 15.86) * mm});
            skLineSegment(sketch, "E491", {"start": v(12.3, 15.86) * mm, "end": v(12.7, 16) * mm});
            skLineSegment(sketch, "E492", {"start": v(12.7, 16) * mm, "end": v(12.98, 16.16) * mm});
            skLineSegment(sketch, "E493", {"start": v(12.98, 16.16) * mm, "end": v(13.24, 16.29) * mm});
            skLineSegment(sketch, "E494", {"start": v(13.24, 16.29) * mm, "end": v(13.35, 16.4) * mm});
            skLineSegment(sketch, "E495", {"start": v(13.35, 16.4) * mm, "end": v(13.3, 16.5) * mm});
            skLineSegment(sketch, "E496", {"start": v(13.3, 16.5) * mm, "end": v(12.93, 16.6) * mm});
            skLineSegment(sketch, "E497", {"start": v(12.93, 16.6) * mm, "end": v(12.49, 16.75) * mm});
            skLineSegment(sketch, "E498", {"start": v(12.49, 16.75) * mm, "end": v(12.1, 16.84) * mm});
            skLineSegment(sketch, "E499", {"start": v(12.1, 16.84) * mm, "end": v(11.73, 17.11) * mm});
            skLineSegment(sketch, "E500", {"start": v(11.73, 17.11) * mm, "end": v(11.5, 17.3) * mm});
            skLineSegment(sketch, "E501", {"start": v(11.5, 17.3) * mm, "end": v(11.2, 17.6) * mm});
            skLineSegment(sketch, "E502", {"start": v(11.2, 17.6) * mm, "end": v(11.1, 17.98) * mm});
            skLineSegment(sketch, "E503", {"start": v(11.1, 17.98) * mm, "end": v(11.1, 18.3) * mm});
            skLineSegment(sketch, "E504", {"start": v(11.1, 18.3) * mm, "end": v(11.13, 18.69) * mm});
            skLineSegment(sketch, "E505", {"start": v(11.13, 18.69) * mm, "end": v(11.2, 18.84) * mm});
            skLineSegment(sketch, "E506", {"start": v(11.2, 18.84) * mm, "end": v(11.33, 18.91) * mm});
            skLineSegment(sketch, "E507", {"start": v(11.33, 18.91) * mm, "end": v(11.42, 18.86) * mm});
            skLineSegment(sketch, "E508", {"start": v(11.42, 18.86) * mm, "end": v(11.54, 18.73) * mm});
            skLineSegment(sketch, "E509", {"start": v(11.54, 18.73) * mm, "end": v(11.72, 18.58) * mm});
            skLineSegment(sketch, "E510", {"start": v(11.72, 18.58) * mm, "end": v(11.94, 18.39) * mm});
            skLineSegment(sketch, "E511", {"start": v(11.94, 18.39) * mm, "end": v(12.19, 18.22) * mm});
            skLineSegment(sketch, "E512", {"start": v(12.19, 18.22) * mm, "end": v(12.44, 18.07) * mm});
            skLineSegment(sketch, "E513", {"start": v(12.44, 18.07) * mm, "end": v(12.72, 17.96) * mm});
            skLineSegment(sketch, "E514", {"start": v(12.72, 17.96) * mm, "end": v(13, 17.91) * mm});
            skLineSegment(sketch, "E515", {"start": v(13, 17.91) * mm, "end": v(13.17, 17.9) * mm});
            skLineSegment(sketch, "E516", {"start": v(13.17, 17.9) * mm, "end": v(13.24, 17.92) * mm});
            skLineSegment(sketch, "E517", {"start": v(13.24, 17.92) * mm, "end": v(13.1, 18.28) * mm});
            skLineSegment(sketch, "E518", {"start": v(13.1, 18.28) * mm, "end": v(13.06, 18.7) * mm});
            skLineSegment(sketch, "E519", {"start": v(13.06, 18.7) * mm, "end": v(13.13, 18.98) * mm});
            skLineSegment(sketch, "E520", {"start": v(13.13, 18.98) * mm, "end": v(13.24, 19.17) * mm});
            skLineSegment(sketch, "E521", {"start": v(13.24, 19.17) * mm, "end": v(13.37, 19.33) * mm});
            skLineSegment(sketch, "E522", {"start": v(13.37, 19.33) * mm, "end": v(13.56, 19.53) * mm});
            skLineSegment(sketch, "E523", {"start": v(13.56, 19.53) * mm, "end": v(13.76, 19.68) * mm});
            skLineSegment(sketch, "E524", {"start": v(13.76, 19.68) * mm, "end": v(14, 19.82) * mm});
            skLineSegment(sketch, "E525", {"start": v(14, 19.82) * mm, "end": v(14.2, 19.92) * mm});
            skLineSegment(sketch, "E526", {"start": v(14.2, 19.92) * mm, "end": v(14.4, 20.02) * mm});
            skLineSegment(sketch, "E527", {"start": v(14.4, 20.02) * mm, "end": v(14.5, 19.93) * mm});
            skLineSegment(sketch, "E528", {"start": v(14.5, 19.93) * mm, "end": v(14.37, 19.45) * mm});
            skLineSegment(sketch, "E529", {"start": v(14.37, 19.45) * mm, "end": v(14.37, 19.1) * mm});
            skLineSegment(sketch, "E530", {"start": v(14.37, 19.1) * mm, "end": v(14.45, 18.77) * mm});
            skLineSegment(sketch, "E531", {"start": v(14.45, 18.77) * mm, "end": v(14.6, 18.52) * mm});
            skLineSegment(sketch, "E532", {"start": v(14.6, 18.52) * mm, "end": v(14.71, 18.4) * mm});
            skLineSegment(sketch, "E533", {"start": v(14.71, 18.4) * mm, "end": v(14.83, 18.3) * mm});
            skLineSegment(sketch, "E534", {"start": v(14.83, 18.3) * mm, "end": v(15.06, 18.18) * mm});
            skLineSegment(sketch, "E535", {"start": v(15.06, 18.18) * mm, "end": v(15.17, 18.16) * mm});
            skLineSegment(sketch, "E536", {"start": v(15.17, 18.16) * mm, "end": v(15.32, 18.12) * mm});
            skLineSegment(sketch, "E537", {"start": v(15.32, 18.12) * mm, "end": v(15.55, 18.13) * mm});
            skLineSegment(sketch, "E538", {"start": v(15.55, 18.13) * mm, "end": v(15.8, 18.19) * mm});
            skLineSegment(sketch, "E539", {"start": v(15.8, 18.19) * mm, "end": v(16.07, 18.3) * mm});
            skLineSegment(sketch, "E540", {"start": v(16.07, 18.3) * mm, "end": v(16.34, 18.43) * mm});
            skLineSegment(sketch, "E541", {"start": v(16.34, 18.43) * mm, "end": v(16.59, 18.58) * mm});
            skLineSegment(sketch, "E542", {"start": v(16.59, 18.58) * mm, "end": v(16.78, 18.68) * mm});
            skLineSegment(sketch, "E543", {"start": v(16.78, 18.68) * mm, "end": v(17.1, 18.87) * mm});
            skLineSegment(sketch, "E544", {"start": v(17.1, 18.87) * mm, "end": v(17.38, 19.01) * mm});
            skLineSegment(sketch, "E545", {"start": v(17.38, 19.01) * mm, "end": v(17.75, 19.2) * mm});
            skLineSegment(sketch, "E546", {"start": v(17.75, 19.2) * mm, "end": v(18.07, 19.34) * mm});
            skLineSegment(sketch, "E547", {"start": v(18.07, 19.34) * mm, "end": v(18.38, 19.47) * mm});
            skLineSegment(sketch, "E548", {"start": v(18.38, 19.47) * mm, "end": v(18.76, 19.56) * mm});
            skLineSegment(sketch, "E549", {"start": v(18.76, 19.56) * mm, "end": v(19.18, 19.58) * mm});
            skLineSegment(sketch, "E550", {"start": v(19.18, 19.58) * mm, "end": v(19.62, 19.53) * mm});
            skLineSegment(sketch, "E551", {"start": v(19.62, 19.53) * mm, "end": v(20.08, 19.42) * mm});
            skLineSegment(sketch, "E552", {"start": v(20.08, 19.42) * mm, "end": v(20.67, 19.3) * mm});
            skLineSegment(sketch, "E553", {"start": v(20.67, 19.3) * mm, "end": v(21.2, 19.22) * mm});
            skLineSegment(sketch, "E554", {"start": v(21.2, 19.22) * mm, "end": v(21.66, 19.18) * mm});
            skLineSegment(sketch, "E555", {"start": v(21.66, 19.18) * mm, "end": v(22.16, 19.17) * mm});
            skLineSegment(sketch, "E556", {"start": v(22.16, 19.17) * mm, "end": v(22.74, 19.14) * mm});
            skLineSegment(sketch, "E557", {"start": v(22.74, 19.14) * mm, "end": v(23.05, 19.15) * mm});
            skLineSegment(sketch, "E558", {"start": v(23.05, 19.15) * mm, "end": v(23.22, 19.21) * mm});
            skLineSegment(sketch, "E559", {"start": v(23.22, 19.21) * mm, "end": v(23.2, 19.55) * mm});
            skLineSegment(sketch, "E560", {"start": v(23.2, 19.55) * mm, "end": v(23.04, 19.81) * mm});
            skLineSegment(sketch, "E561", {"start": v(23.04, 19.81) * mm, "end": v(22.86, 20.08) * mm});
            skLineSegment(sketch, "E562", {"start": v(22.86, 20.08) * mm, "end": v(22.6, 20.2) * mm});
            skLineSegment(sketch, "E563", {"start": v(22.6, 20.2) * mm, "end": v(22.26, 20.35) * mm});
            skLineSegment(sketch, "E564", {"start": v(22.26, 20.35) * mm, "end": v(21.89, 20.46) * mm});
            skLineSegment(sketch, "E565", {"start": v(21.89, 20.46) * mm, "end": v(21.37, 20.6) * mm});
            skLineSegment(sketch, "E566", {"start": v(21.37, 20.6) * mm, "end": v(21, 20.65) * mm});
            skLineSegment(sketch, "E567", {"start": v(21, 20.65) * mm, "end": v(20.68, 20.77) * mm});
            skLineSegment(sketch, "E568", {"start": v(20.68, 20.77) * mm, "end": v(20.2, 20.93) * mm});
            skLineSegment(sketch, "E569", {"start": v(20.2, 20.93) * mm, "end": v(19.89, 21.13) * mm});
            skLineSegment(sketch, "E570", {"start": v(19.89, 21.13) * mm, "end": v(19.56, 21.29) * mm});
            skLineSegment(sketch, "E571", {"start": v(19.56, 21.29) * mm, "end": v(19.05, 21.54) * mm});
            skLineSegment(sketch, "E572", {"start": v(19.05, 21.54) * mm, "end": v(18.63, 21.81) * mm});
            skLineSegment(sketch, "E573", {"start": v(18.63, 21.81) * mm, "end": v(18.27, 22.12) * mm});
            skLineSegment(sketch, "E574", {"start": v(18.27, 22.12) * mm, "end": v(17.98, 22.44) * mm});
            skLineSegment(sketch, "E575", {"start": v(17.98, 22.44) * mm, "end": v(17.85, 22.63) * mm});
            skLineSegment(sketch, "E576", {"start": v(17.85, 22.63) * mm, "end": v(17.8, 22.72) * mm});
            skLineSegment(sketch, "E577", {"start": v(17.8, 22.72) * mm, "end": v(17.63, 22.74) * mm});
            skLineSegment(sketch, "E578", {"start": v(17.63, 22.74) * mm, "end": v(17.4, 22.65) * mm});
            skLineSegment(sketch, "E579", {"start": v(17.4, 22.65) * mm, "end": v(17.22, 22.56) * mm});
            skLineSegment(sketch, "E580", {"start": v(17.22, 22.56) * mm, "end": v(17.05, 22.49) * mm});
            skLineSegment(sketch, "E581", {"start": v(17.05, 22.49) * mm, "end": v(16.84, 22.41) * mm});
            skLineSegment(sketch, "E582", {"start": v(16.84, 22.41) * mm, "end": v(16.57, 22.3) * mm});
            skLineSegment(sketch, "E583", {"start": v(16.57, 22.3) * mm, "end": v(16.36, 22.23) * mm});
            skLineSegment(sketch, "E584", {"start": v(16.36, 22.23) * mm, "end": v(16.14, 22.16) * mm});
            skLineSegment(sketch, "E585", {"start": v(16.14, 22.16) * mm, "end": v(16, 22.12) * mm});
            skLineSegment(sketch, "E586", {"start": v(16, 22.12) * mm, "end": v(15.72, 22.28) * mm});
            skLineSegment(sketch, "E587", {"start": v(15.72, 22.28) * mm, "end": v(15.6, 22.36) * mm});
            skLineSegment(sketch, "E588", {"start": v(15.6, 22.36) * mm, "end": v(15.45, 22.36) * mm});
            skLineSegment(sketch, "E589", {"start": v(15.45, 22.36) * mm, "end": v(15.3, 22.3) * mm});
            skLineSegment(sketch, "E590", {"start": v(15.3, 22.3) * mm, "end": v(15.08, 22.3) * mm});
            skLineSegment(sketch, "E591", {"start": v(15.08, 22.3) * mm, "end": v(14.87, 22.31) * mm});
            skLineSegment(sketch, "E592", {"start": v(14.87, 22.31) * mm, "end": v(14.74, 22.35) * mm});
            skLineSegment(sketch, "E593", {"start": v(14.74, 22.35) * mm, "end": v(14.21, 22.35) * mm});
            skLineSegment(sketch, "E594", {"start": v(14.21, 22.35) * mm, "end": v(14.17, 22.33) * mm});
            skLineSegment(sketch, "E595", {"start": v(14.17, 22.33) * mm, "end": v(14.17, 22.18) * mm});
            skLineSegment(sketch, "E596", {"start": v(14.17, 22.18) * mm, "end": v(14.16, 22.06) * mm});
            skLineSegment(sketch, "E597", {"start": v(14.16, 22.06) * mm, "end": v(14.13, 21.9) * mm});
            skLineSegment(sketch, "E598", {"start": v(14.13, 21.9) * mm, "end": v(14.07, 21.78) * mm});
            skLineSegment(sketch, "E599", {"start": v(14.07, 21.78) * mm, "end": v(13.96, 21.7) * mm});
            skLineSegment(sketch, "E600", {"start": v(13.96, 21.7) * mm, "end": v(13.8, 21.64) * mm});
            skLineSegment(sketch, "E601", {"start": v(13.8, 21.64) * mm, "end": v(13.62, 21.64) * mm});
            skLineSegment(sketch, "E602", {"start": v(13.62, 21.64) * mm, "end": v(13.4, 21.7) * mm});
            skLineSegment(sketch, "E603", {"start": v(13.4, 21.7) * mm, "end": v(13.31, 21.76) * mm});
            skLineSegment(sketch, "E604", {"start": v(13.31, 21.76) * mm, "end": v(13.16, 21.83) * mm});
            skLineSegment(sketch, "E605", {"start": v(13.16, 21.83) * mm, "end": v(13.06, 21.9) * mm});
            skLineSegment(sketch, "E606", {"start": v(13.06, 21.9) * mm, "end": v(13, 21.94) * mm});
            skLineSegment(sketch, "E607", {"start": v(13, 21.94) * mm, "end": v(13.02, 21.8) * mm});
            skLineSegment(sketch, "E608", {"start": v(13.02, 21.8) * mm, "end": v(13.1, 21.7) * mm});
            skLineSegment(sketch, "E609", {"start": v(13.1, 21.7) * mm, "end": v(13.16, 21.61) * mm});
            skLineSegment(sketch, "E610", {"start": v(13.16, 21.61) * mm, "end": v(13.25, 21.5) * mm});
            skLineSegment(sketch, "E611", {"start": v(13.25, 21.5) * mm, "end": v(13.35, 21.35) * mm});
            skLineSegment(sketch, "E612", {"start": v(13.35, 21.35) * mm, "end": v(13.4, 21.3) * mm});
            skLineSegment(sketch, "E613", {"start": v(13.4, 21.3) * mm, "end": v(13.43, 21.23) * mm});
            skLineSegment(sketch, "E614", {"start": v(13.43, 21.23) * mm, "end": v(13.4, 21.16) * mm});
            skLineSegment(sketch, "E615", {"start": v(13.4, 21.16) * mm, "end": v(13.3, 21.1) * mm});
            skLineSegment(sketch, "E616", {"start": v(13.3, 21.1) * mm, "end": v(13.06, 21.05) * mm});
            skLineSegment(sketch, "E617", {"start": v(13.06, 21.05) * mm, "end": v(12.8, 21.05) * mm});
            skLineSegment(sketch, "E618", {"start": v(12.8, 21.05) * mm, "end": v(12.57, 21.12) * mm});
            skLineSegment(sketch, "E619", {"start": v(12.57, 21.12) * mm, "end": v(12.39, 21.24) * mm});
            skLineSegment(sketch, "E620", {"start": v(12.39, 21.24) * mm, "end": v(12.2, 21.35) * mm});
            skLineSegment(sketch, "E621", {"start": v(12.2, 21.35) * mm, "end": v(12.09, 21.46) * mm});
            skLineSegment(sketch, "E622", {"start": v(12.09, 21.46) * mm, "end": v(12.03, 21.46) * mm});
            skLineSegment(sketch, "E623", {"start": v(12.03, 21.46) * mm, "end": v(12.04, 21.35) * mm});
            skLineSegment(sketch, "E624", {"start": v(12.04, 21.35) * mm, "end": v(12.1, 21.23) * mm});
            skLineSegment(sketch, "E625", {"start": v(12.1, 21.23) * mm, "end": v(12.11, 21.12) * mm});
            skLineSegment(sketch, "E626", {"start": v(12.11, 21.12) * mm, "end": v(12.09, 21.01) * mm});
            skLineSegment(sketch, "E627", {"start": v(12.09, 21.01) * mm, "end": v(12.03, 20.9) * mm});
            skLineSegment(sketch, "E628", {"start": v(12.03, 20.9) * mm, "end": v(11.92, 20.87) * mm});
            skLineSegment(sketch, "E629", {"start": v(11.92, 20.87) * mm, "end": v(11.73, 20.88) * mm});
            skLineSegment(sketch, "E630", {"start": v(11.73, 20.88) * mm, "end": v(11.53, 20.96) * mm});
            skLineSegment(sketch, "E631", {"start": v(11.53, 20.96) * mm, "end": v(11.34, 21.05) * mm});
            skLineSegment(sketch, "E632", {"start": v(11.34, 21.05) * mm, "end": v(11.14, 21.17) * mm});
            skLineSegment(sketch, "E633", {"start": v(11.14, 21.17) * mm, "end": v(11, 21.26) * mm});
            skLineSegment(sketch, "E634", {"start": v(11, 21.26) * mm, "end": v(10.8, 21.32) * mm});
            skLineSegment(sketch, "E635", {"start": v(10.8, 21.32) * mm, "end": v(10.73, 21.33) * mm});
            skLineSegment(sketch, "E636", {"start": v(10.73, 21.33) * mm, "end": v(10.83, 21.16) * mm});
            skLineSegment(sketch, "E637", {"start": v(10.83, 21.16) * mm, "end": v(10.87, 21.01) * mm});
            skLineSegment(sketch, "E638", {"start": v(10.87, 21.01) * mm, "end": v(10.85, 20.86) * mm});
            skLineSegment(sketch, "E639", {"start": v(10.85, 20.86) * mm, "end": v(10.79, 20.77) * mm});
            skLineSegment(sketch, "E640", {"start": v(10.79, 20.77) * mm, "end": v(10.66, 20.74) * mm});
            skLineSegment(sketch, "E641", {"start": v(10.66, 20.74) * mm, "end": v(10.53, 20.78) * mm});
            skLineSegment(sketch, "E642", {"start": v(10.53, 20.78) * mm, "end": v(10.33, 20.87) * mm});
            skLineSegment(sketch, "E643", {"start": v(10.33, 20.87) * mm, "end": v(10.18, 20.95) * mm});
            skLineSegment(sketch, "E644", {"start": v(10.18, 20.95) * mm, "end": v(10, 21.07) * mm});
            skLineSegment(sketch, "E645", {"start": v(10, 21.07) * mm, "end": v(9.84, 21.18) * mm});
            skLineSegment(sketch, "E646", {"start": v(9.84, 21.18) * mm, "end": v(9.72, 21.28) * mm});
            skLineSegment(sketch, "E647", {"start": v(9.72, 21.28) * mm, "end": v(9.61, 21.34) * mm});
            skLineSegment(sketch, "E648", {"start": v(9.61, 21.34) * mm, "end": v(9.56, 21.29) * mm});
            skLineSegment(sketch, "E649", {"start": v(9.56, 21.29) * mm, "end": v(9.64, 21.13) * mm});
            skLineSegment(sketch, "E650", {"start": v(9.64, 21.13) * mm, "end": v(9.66, 20.99) * mm});
            skLineSegment(sketch, "E651", {"start": v(9.66, 20.99) * mm, "end": v(9.66, 20.9) * mm});
            skLineSegment(sketch, "E652", {"start": v(9.66, 20.9) * mm, "end": v(9.61, 20.74) * mm});
            skLineSegment(sketch, "E653", {"start": v(9.61, 20.74) * mm, "end": v(9.51, 20.63) * mm});
            skLineSegment(sketch, "E654", {"start": v(9.51, 20.63) * mm, "end": v(9.33, 20.55) * mm});
            skLineSegment(sketch, "E655", {"start": v(9.33, 20.55) * mm, "end": v(9.17, 20.56) * mm});
            skLineSegment(sketch, "E656", {"start": v(9.17, 20.56) * mm, "end": v(8.9, 20.58) * mm});
            skLineSegment(sketch, "E657", {"start": v(8.9, 20.58) * mm, "end": v(8.7, 20.65) * mm});
            skLineSegment(sketch, "E658", {"start": v(8.7, 20.65) * mm, "end": v(8.52, 20.73) * mm});
            skLineSegment(sketch, "E659", {"start": v(8.52, 20.73) * mm, "end": v(8.36, 20.73) * mm});
            skLineSegment(sketch, "E660", {"start": v(8.36, 20.73) * mm, "end": v(8.23, 20.62) * mm});
            skLineSegment(sketch, "E661", {"start": v(8.23, 20.62) * mm, "end": v(8.15, 20.45) * mm});
            skLineSegment(sketch, "E662", {"start": v(8.15, 20.45) * mm, "end": v(8.05, 20.31) * mm});
            skLineSegment(sketch, "E663", {"start": v(8.05, 20.31) * mm, "end": v(7.89, 20.13) * mm});
            skLineSegment(sketch, "E664", {"start": v(7.89, 20.13) * mm, "end": v(7.78, 20) * mm});
            skLineSegment(sketch, "E665", {"start": v(7.78, 20) * mm, "end": v(7.69, 19.89) * mm});
            skLineSegment(sketch, "E666", {"start": v(7.69, 19.89) * mm, "end": v(7.63, 19.73) * mm});
            skLineSegment(sketch, "E667", {"start": v(7.63, 19.73) * mm, "end": v(7.6, 19.5) * mm});
            skLineSegment(sketch, "E668", {"start": v(7.6, 19.5) * mm, "end": v(7.54, 19.36) * mm});
            skLineSegment(sketch, "E669", {"start": v(7.54, 19.36) * mm, "end": v(7.44, 19.18) * mm});
            skLineSegment(sketch, "E670", {"start": v(7.44, 19.18) * mm, "end": v(7.35, 19.02) * mm});
            skLineSegment(sketch, "E671", {"start": v(7.35, 19.02) * mm, "end": v(7.2, 18.76) * mm});
            skLineSegment(sketch, "E672", {"start": v(7.2, 18.76) * mm, "end": v(7.04, 18.56) * mm});
            skLineSegment(sketch, "E673", {"start": v(7.04, 18.56) * mm, "end": v(6.83, 18.36) * mm});
            skLineSegment(sketch, "E674", {"start": v(6.83, 18.36) * mm, "end": v(6.64, 18.25) * mm});
            skLineSegment(sketch, "E675", {"start": v(6.64, 18.25) * mm, "end": v(6.45, 18.2) * mm});
            skLineSegment(sketch, "E676", {"start": v(6.45, 18.2) * mm, "end": v(6.2, 18.22) * mm});
            skLineSegment(sketch, "E677", {"start": v(6.2, 18.22) * mm, "end": v(6.06, 18.25) * mm});
            skLineSegment(sketch, "E678", {"start": v(6.06, 18.25) * mm, "end": v(6.13, 18.5) * mm});
            skLineSegment(sketch, "E679", {"start": v(6.13, 18.5) * mm, "end": v(6.27, 18.7) * mm});
            skLineSegment(sketch, "E680", {"start": v(6.27, 18.7) * mm, "end": v(6.4, 18.98) * mm});
            skLineSegment(sketch, "E681", {"start": v(6.4, 18.98) * mm, "end": v(6.45, 19.17) * mm});
            skLineSegment(sketch, "E682", {"start": v(6.45, 19.17) * mm, "end": v(6.46, 19.32) * mm});
            skLineSegment(sketch, "E683", {"start": v(6.46, 19.32) * mm, "end": v(6.52, 19.54) * mm});
            skLineSegment(sketch, "E684", {"start": v(6.52, 19.54) * mm, "end": v(6.5, 19.82) * mm});
            skLineSegment(sketch, "E685", {"start": v(6.5, 19.82) * mm, "end": v(6.4, 19.9) * mm});
            skLineSegment(sketch, "E686", {"start": v(6.4, 19.9) * mm, "end": v(6.35, 20.07) * mm});
            skLineSegment(sketch, "E687", {"start": v(6.35, 20.07) * mm, "end": v(6.4, 20.37) * mm});
            skLineSegment(sketch, "E688", {"start": v(6.4, 20.37) * mm, "end": v(6.43, 20.7) * mm});
            skLineSegment(sketch, "E689", {"start": v(6.43, 20.7) * mm, "end": v(6.36, 20.88) * mm});
            skLineSegment(sketch, "E690", {"start": v(6.36, 20.88) * mm, "end": v(6.24, 20.98) * mm});
            skLineSegment(sketch, "E691", {"start": v(6.24, 20.98) * mm, "end": v(6.09, 20.93) * mm});
            skLineSegment(sketch, "E692", {"start": v(6.09, 20.93) * mm, "end": v(5.87, 20.75) * mm});
            skLineSegment(sketch, "E693", {"start": v(5.87, 20.75) * mm, "end": v(5.72, 20.59) * mm});
            skLineSegment(sketch, "E694", {"start": v(5.72, 20.59) * mm, "end": v(5.55, 20.4) * mm});
            skLineSegment(sketch, "E695", {"start": v(5.55, 20.4) * mm, "end": v(5.46, 20.16) * mm});
            skLineSegment(sketch, "E696", {"start": v(5.46, 20.16) * mm, "end": v(5.32, 19.85) * mm});
            skLineSegment(sketch, "E697", {"start": v(5.32, 19.85) * mm, "end": v(5.34, 19.58) * mm});
            skLineSegment(sketch, "E698", {"start": v(5.34, 19.58) * mm, "end": v(5.26, 19.3) * mm});
            skLineSegment(sketch, "E699", {"start": v(5.26, 19.3) * mm, "end": v(5.23, 19.01) * mm});
            skLineSegment(sketch, "E700", {"start": v(5.23, 19.01) * mm, "end": v(5.24, 18.73) * mm});
            skLineSegment(sketch, "E701", {"start": v(5.24, 18.73) * mm, "end": v(5.16, 18.57) * mm});
            skLineSegment(sketch, "E702", {"start": v(5.16, 18.57) * mm, "end": v(5.08, 18.44) * mm});
            skLineSegment(sketch, "E703", {"start": v(5.08, 18.44) * mm, "end": v(4.98, 18.4) * mm});
            skLineSegment(sketch, "E704", {"start": v(4.98, 18.4) * mm, "end": v(4.86, 18.39) * mm});
            skLineSegment(sketch, "E705", {"start": v(4.86, 18.39) * mm, "end": v(4.72, 18.32) * mm});
            skLineSegment(sketch, "E706", {"start": v(4.72, 18.32) * mm, "end": v(4.57, 18.24) * mm});
            skLineSegment(sketch, "E707", {"start": v(4.57, 18.24) * mm, "end": v(4.49, 18.15) * mm});
            skLineSegment(sketch, "E708", {"start": v(4.49, 18.15) * mm, "end": v(4.32, 17.95) * mm});
            skLineSegment(sketch, "E709", {"start": v(4.32, 17.95) * mm, "end": v(4.19, 17.73) * mm});
            skLineSegment(sketch, "E710", {"start": v(4.19, 17.73) * mm, "end": v(3.99, 17.34) * mm});
            skLineSegment(sketch, "E711", {"start": v(3.99, 17.34) * mm, "end": v(3.95, 17.2) * mm});
            skLineSegment(sketch, "E712", {"start": v(3.95, 17.2) * mm, "end": v(3.84, 17.03) * mm});
            skLineSegment(sketch, "E713", {"start": v(3.84, 17.03) * mm, "end": v(3.78, 16.9) * mm});
            skLineSegment(sketch, "E714", {"start": v(3.78, 16.9) * mm, "end": v(3.72, 16.8) * mm});
            skLineSegment(sketch, "E715", {"start": v(3.72, 16.8) * mm, "end": v(3.6, 16.78) * mm});
            skLineSegment(sketch, "E716", {"start": v(3.6, 16.78) * mm, "end": v(3.47, 16.8) * mm});
            skLineSegment(sketch, "E717", {"start": v(3.47, 16.8) * mm, "end": v(3.3, 17.04) * mm});
            skLineSegment(sketch, "E718", {"start": v(3.3, 17.04) * mm, "end": v(3.2, 17.36) * mm});
            skLineSegment(sketch, "E719", {"start": v(3.2, 17.36) * mm, "end": v(3.17, 17.7) * mm});
            skLineSegment(sketch, "E720", {"start": v(3.17, 17.7) * mm, "end": v(3.17, 17.96) * mm});
            skLineSegment(sketch, "E721", {"start": v(3.17, 17.96) * mm, "end": v(3.17, 18.26) * mm});
            skLineSegment(sketch, "E722", {"start": v(3.17, 18.26) * mm, "end": v(3.24, 18.46) * mm});
            skLineSegment(sketch, "E723", {"start": v(3.24, 18.46) * mm, "end": v(3.32, 18.69) * mm});
            skLineSegment(sketch, "E724", {"start": v(3.32, 18.69) * mm, "end": v(3.44, 18.86) * mm});
            skLineSegment(sketch, "E725", {"start": v(3.44, 18.86) * mm, "end": v(3.47, 19) * mm});
            skLineSegment(sketch, "E726", {"start": v(3.47, 19) * mm, "end": v(3.57, 19.1) * mm});
            skLineSegment(sketch, "E727", {"start": v(3.57, 19.1) * mm, "end": v(3.59, 19.45) * mm});
            skLineSegment(sketch, "E728", {"start": v(3.59, 19.45) * mm, "end": v(3.64, 19.6) * mm});
            skLineSegment(sketch, "E729", {"start": v(3.64, 19.6) * mm, "end": v(3.74, 19.73) * mm});
            skLineSegment(sketch, "E730", {"start": v(3.74, 19.73) * mm, "end": v(3.85, 19.93) * mm});
            skLineSegment(sketch, "E731", {"start": v(3.85, 19.93) * mm, "end": v(3.97, 20.1) * mm});
            skLineSegment(sketch, "E732", {"start": v(3.97, 20.1) * mm, "end": v(4.08, 20.23) * mm});
            skLineSegment(sketch, "E733", {"start": v(4.08, 20.23) * mm, "end": v(4.15, 20.39) * mm});
            skLineSegment(sketch, "E734", {"start": v(4.15, 20.39) * mm, "end": v(4.2, 20.53) * mm});
            skLineSegment(sketch, "E735", {"start": v(4.2, 20.53) * mm, "end": v(4.17, 20.73) * mm});
            skLineSegment(sketch, "E736", {"start": v(4.17, 20.73) * mm, "end": v(4.13, 20.86) * mm});
            skLineSegment(sketch, "E737", {"start": v(4.13, 20.86) * mm, "end": v(4.01, 20.88) * mm});
            skLineSegment(sketch, "E738", {"start": v(4.01, 20.88) * mm, "end": v(3.88, 20.78) * mm});
            skLineSegment(sketch, "E739", {"start": v(3.88, 20.78) * mm, "end": v(3.6, 20.68) * mm});
            skLineSegment(sketch, "E740", {"start": v(3.6, 20.68) * mm, "end": v(3.4, 20.58) * mm});
            skLineSegment(sketch, "E741", {"start": v(3.4, 20.58) * mm, "end": v(3.19, 20.46) * mm});
            skLineSegment(sketch, "E742", {"start": v(3.19, 20.46) * mm, "end": v(2.98, 20.28) * mm});
            skLineSegment(sketch, "E743", {"start": v(2.98, 20.28) * mm, "end": v(2.8, 20.11) * mm});
            skLineSegment(sketch, "E744", {"start": v(2.8, 20.11) * mm, "end": v(2.6, 19.95) * mm});
            skLineSegment(sketch, "E745", {"start": v(2.6, 19.95) * mm, "end": v(2.5, 19.77) * mm});
            skLineSegment(sketch, "E746", {"start": v(2.5, 19.77) * mm, "end": v(2.37, 19.68) * mm});
            skLineSegment(sketch, "E747", {"start": v(2.37, 19.68) * mm, "end": v(2.26, 19.6) * mm});
            skLineSegment(sketch, "E748", {"start": v(2.26, 19.6) * mm, "end": v(2.08, 19.6) * mm});
            skLineSegment(sketch, "E749", {"start": v(2.08, 19.6) * mm, "end": v(1.87, 19.6) * mm});
            skLineSegment(sketch, "E750", {"start": v(1.87, 19.6) * mm, "end": v(1.74, 19.56) * mm});
            skLineSegment(sketch, "E751", {"start": v(1.74, 19.56) * mm, "end": v(1.62, 19.4) * mm});
            skLineSegment(sketch, "E752", {"start": v(1.62, 19.4) * mm, "end": v(1.47, 19.26) * mm});
            skLineSegment(sketch, "E753", {"start": v(1.47, 19.26) * mm, "end": v(1.32, 19.12) * mm});
            skLineSegment(sketch, "E754", {"start": v(1.32, 19.12) * mm, "end": v(1.17, 18.96) * mm});
            skLineSegment(sketch, "E755", {"start": v(1.17, 18.96) * mm, "end": v(1.06, 18.8) * mm});
            skLineSegment(sketch, "E756", {"start": v(1.06, 18.8) * mm, "end": v(0.92, 18.64) * mm});
            skLineSegment(sketch, "E757", {"start": v(0.92, 18.64) * mm, "end": v(0.8, 18.5) * mm});
            skLineSegment(sketch, "E758", {"start": v(0.8, 18.5) * mm, "end": v(0.75, 18.36) * mm});
            skLineSegment(sketch, "E759", {"start": v(0.75, 18.36) * mm, "end": v(0.59, 18.1) * mm});
            skLineSegment(sketch, "E760", {"start": v(0.59, 18.1) * mm, "end": v(0.5, 18.14) * mm});
            skLineSegment(sketch, "E761", {"start": v(0.5, 18.14) * mm, "end": v(0.36, 18.27) * mm});
            skLineSegment(sketch, "E762", {"start": v(0.36, 18.27) * mm, "end": v(0.27, 18.42) * mm});
            skLineSegment(sketch, "E763", {"start": v(0.27, 18.42) * mm, "end": v(0.14, 18.76) * mm});
            skLineSegment(sketch, "E764", {"start": v(0.14, 18.76) * mm, "end": v(0.1, 19.27) * mm});
            skLineSegment(sketch, "E765", {"start": v(0.1, 19.27) * mm, "end": v(0.13, 19.5) * mm});
            skLineSegment(sketch, "E766", {"start": v(0.13, 19.5) * mm, "end": v(0.2, 19.67) * mm});
            skLineSegment(sketch, "E767", {"start": v(0.2, 19.67) * mm, "end": v(0.25, 19.85) * mm});
            skLineSegment(sketch, "E768", {"start": v(0.25, 19.85) * mm, "end": v(0.34, 20.01) * mm});
            skLineSegment(sketch, "E769", {"start": v(0.34, 20.01) * mm, "end": v(0.44, 20.15) * mm});
            skLineSegment(sketch, "E770", {"start": v(0.44, 20.15) * mm, "end": v(0.54, 20.26) * mm});
            skLineSegment(sketch, "E771", {"start": v(0.54, 20.26) * mm, "end": v(0.66, 20.36) * mm});
            skLineSegment(sketch, "E772", {"start": v(0.66, 20.36) * mm, "end": v(0.72, 20.48) * mm});
            skLineSegment(sketch, "E773", {"start": v(0.72, 20.48) * mm, "end": v(0.72, 20.61) * mm});
            skLineSegment(sketch, "E774", {"start": v(0.72, 20.61) * mm, "end": v(0.72, 20.83) * mm});
            skLineSegment(sketch, "E775", {"start": v(0.72, 20.83) * mm, "end": v(0.79, 21) * mm});
            skLineSegment(sketch, "E776", {"start": v(0.79, 21) * mm, "end": v(0.9, 21.07) * mm});
            skLineSegment(sketch, "E777", {"start": v(0.9, 21.07) * mm, "end": v(1.11, 21.13) * mm});
            skLineSegment(sketch, "E778", {"start": v(1.11, 21.13) * mm, "end": v(1.2, 21.13) * mm});
            skLineSegment(sketch, "E779", {"start": v(1.2, 21.13) * mm, "end": v(1.37, 21.13) * mm});
            skLineSegment(sketch, "E780", {"start": v(1.37, 21.13) * mm, "end": v(1.52, 21.16) * mm});
            skLineSegment(sketch, "E781", {"start": v(1.52, 21.16) * mm, "end": v(1.8, 21.26) * mm});
            skLineSegment(sketch, "E782", {"start": v(1.8, 21.26) * mm, "end": v(2.03, 21.37) * mm});
            skLineSegment(sketch, "E783", {"start": v(2.03, 21.37) * mm, "end": v(2.38, 21.57) * mm});
            skLineSegment(sketch, "E784", {"start": v(2.38, 21.57) * mm, "end": v(2.75, 21.76) * mm});
            skLineSegment(sketch, "E785", {"start": v(2.75, 21.76) * mm, "end": v(3.06, 21.95) * mm});
            skLineSegment(sketch, "E786", {"start": v(3.06, 21.95) * mm, "end": v(3.1, 22.05) * mm});
            skLineSegment(sketch, "E787", {"start": v(3.1, 22.05) * mm, "end": v(3.02, 22.05) * mm});
            skLineSegment(sketch, "E788", {"start": v(3.02, 22.05) * mm, "end": v(2.79, 22.06) * mm});
            skLineSegment(sketch, "E789", {"start": v(2.79, 22.06) * mm, "end": v(2.48, 22.18) * mm});
            skLineSegment(sketch, "E790", {"start": v(2.48, 22.18) * mm, "end": v(2.23, 22.28) * mm});
            skLineSegment(sketch, "E791", {"start": v(2.23, 22.28) * mm, "end": v(2.03, 22.4) * mm});
            skLineSegment(sketch, "E792", {"start": v(2.03, 22.4) * mm, "end": v(1.8, 22.47) * mm});
            skLineSegment(sketch, "E793", {"start": v(1.8, 22.47) * mm, "end": v(1.55, 22.47) * mm});
            skLineSegment(sketch, "E794", {"start": v(1.55, 22.47) * mm, "end": v(1.2, 22.44) * mm});
            skLineSegment(sketch, "E795", {"start": v(1.2, 22.44) * mm, "end": v(0.87, 22.33) * mm});
            skLineSegment(sketch, "E796", {"start": v(0.87, 22.33) * mm, "end": v(0.66, 22.24) * mm});
            skLineSegment(sketch, "E797", {"start": v(0.66, 22.24) * mm, "end": v(0.51, 22.18) * mm});
            skLineSegment(sketch, "E798", {"start": v(0.51, 22.18) * mm, "end": v(0.43, 22.12) * mm});
            skLineSegment(sketch, "E799", {"start": v(0.43, 22.12) * mm, "end": v(0.35, 22.08) * mm});
            skLineSegment(sketch, "E800", {"start": v(0.35, 22.08) * mm, "end": v(0.24, 22.16) * mm});
            skLineSegment(sketch, "E801", {"start": v(0.24, 22.16) * mm, "end": v(0.15, 22.3) * mm});
            skLineSegment(sketch, "E802", {"start": v(0.15, 22.3) * mm, "end": v(0.14, 22.47) * mm});
            skLineSegment(sketch, "E803", {"start": v(0.14, 22.47) * mm, "end": v(0.16, 22.64) * mm});
            skLineSegment(sketch, "E804", {"start": v(0.16, 22.64) * mm, "end": v(0.17, 22.77) * mm});
            skLineSegment(sketch, "E805", {"start": v(0.17, 22.77) * mm, "end": v(0.26, 22.95) * mm});
            skLineSegment(sketch, "E806", {"start": v(0.26, 22.95) * mm, "end": v(0.39, 23.12) * mm});
            skLineSegment(sketch, "E807", {"start": v(0.39, 23.12) * mm, "end": v(0.51, 23.24) * mm});
            skLineSegment(sketch, "E808", {"start": v(0.51, 23.24) * mm, "end": v(0.68, 23.36) * mm});
            skLineSegment(sketch, "E809", {"start": v(0.68, 23.36) * mm, "end": v(0.94, 23.5) * mm});
            skLineSegment(sketch, "E810", {"start": v(0.94, 23.5) * mm, "end": v(1.16, 23.6) * mm});
            skLineSegment(sketch, "E811", {"start": v(1.16, 23.6) * mm, "end": v(1.37, 23.62) * mm});
            skLineSegment(sketch, "E812", {"start": v(1.37, 23.62) * mm, "end": v(1.7, 23.64) * mm});
            skLineSegment(sketch, "E813", {"start": v(1.7, 23.64) * mm, "end": v(1.99, 23.65) * mm});
            skLineSegment(sketch, "E814", {"start": v(1.99, 23.65) * mm, "end": v(2.1, 23.72) * mm});
            skLineSegment(sketch, "E815", {"start": v(2.1, 23.72) * mm, "end": v(2.58, 23.74) * mm});
            skLineSegment(sketch, "E816", {"start": v(2.58, 23.74) * mm, "end": v(3.05, 23.6) * mm});
            skLineSegment(sketch, "E817", {"start": v(3.05, 23.6) * mm, "end": v(3.35, 23.47) * mm});
            skLineSegment(sketch, "E818", {"start": v(3.35, 23.47) * mm, "end": v(3.68, 23.35) * mm});
            skLineSegment(sketch, "E819", {"start": v(3.68, 23.35) * mm, "end": v(3.92, 23.26) * mm});
            skLineSegment(sketch, "E820", {"start": v(3.92, 23.26) * mm, "end": v(4.2, 23.2) * mm});
            skLineSegment(sketch, "E821", {"start": v(4.2, 23.2) * mm, "end": v(4.45, 23.15) * mm});
            skLineSegment(sketch, "E822", {"start": v(4.45, 23.15) * mm, "end": v(5.08, 23.16) * mm});
            skLineSegment(sketch, "E823", {"start": v(5.08, 23.16) * mm, "end": v(5.37, 23.21) * mm});
            skLineSegment(sketch, "E824", {"start": v(5.37, 23.21) * mm, "end": v(5.71, 23.3) * mm});
            skLineSegment(sketch, "E825", {"start": v(5.71, 23.3) * mm, "end": v(6.19, 23.44) * mm});
            skLineSegment(sketch, "E826", {"start": v(6.19, 23.44) * mm, "end": v(6.64, 23.59) * mm});
            skLineSegment(sketch, "E827", {"start": v(6.64, 23.59) * mm, "end": v(6.83, 23.69) * mm});
            skLineSegment(sketch, "E828", {"start": v(6.83, 23.69) * mm, "end": v(7.08, 23.78) * mm});
            skLineSegment(sketch, "E829", {"start": v(7.08, 23.78) * mm, "end": v(7.44, 23.97) * mm});
            skLineSegment(sketch, "E830", {"start": v(7.44, 23.97) * mm, "end": v(7.77, 24.13) * mm});
            skLineSegment(sketch, "E831", {"start": v(7.77, 24.13) * mm, "end": v(8.13, 24.36) * mm});
            skLineSegment(sketch, "E832", {"start": v(8.13, 24.36) * mm, "end": v(8.5, 24.62) * mm});
            skLineSegment(sketch, "E833", {"start": v(8.5, 24.62) * mm, "end": v(8.9, 24.85) * mm});
            skLineSegment(sketch, "E834", {"start": v(8.9, 24.85) * mm, "end": v(9.17, 25.06) * mm});
            skLineSegment(sketch, "E835", {"start": v(9.17, 25.06) * mm, "end": v(9.5, 25.26) * mm});
            skLineSegment(sketch, "E836", {"start": v(9.5, 25.26) * mm, "end": v(9.85, 25.53) * mm});
            skLineSegment(sketch, "E837", {"start": v(9.85, 25.53) * mm, "end": v(10.16, 25.73) * mm});
            skLineSegment(sketch, "E838", {"start": v(10.16, 25.73) * mm, "end": v(10.5, 26) * mm});
            skLineSegment(sketch, "E839", {"start": v(10.5, 26) * mm, "end": v(10.74, 26.17) * mm});
            skLineSegment(sketch, "E840", {"start": v(10.74, 26.17) * mm, "end": v(11.27, 26.57) * mm});
            skLineSegment(sketch, "E841", {"start": v(11.27, 26.57) * mm, "end": v(11.77, 26.87) * mm});
            skLineSegment(sketch, "E842", {"start": v(11.77, 26.87) * mm, "end": v(12.26, 27.16) * mm});
            skLineSegment(sketch, "E843", {"start": v(12.26, 27.16) * mm, "end": v(12.59, 27.45) * mm});
            skLineSegment(sketch, "E844", {"start": v(12.59, 27.45) * mm, "end": v(12.65, 27.55) * mm});
            skLineSegment(sketch, "E845", {"start": v(12.65, 27.55) * mm, "end": v(12.45, 27.78) * mm});
            skLineSegment(sketch, "E846", {"start": v(12.45, 27.78) * mm, "end": v(12.04, 28.12) * mm});
            skLineSegment(sketch, "E847", {"start": v(12.04, 28.12) * mm, "end": v(11.42, 28.79) * mm});
            skLineSegment(sketch, "E848", {"start": v(11.42, 28.79) * mm, "end": v(10.79, 29.6) * mm});
            skLineSegment(sketch, "E849", {"start": v(10.79, 29.6) * mm, "end": v(10.33, 30.22) * mm});
            skLineSegment(sketch, "E850", {"start": v(10.33, 30.22) * mm, "end": v(10.19, 30.25) * mm});
            skLineSegment(sketch, "E851", {"start": v(10.19, 30.25) * mm, "end": v(9.99, 30.39) * mm});
            skLineSegment(sketch, "E852", {"start": v(9.99, 30.39) * mm, "end": v(9.98, 30.51) * mm});
            skLineSegment(sketch, "E853", {"start": v(9.98, 30.51) * mm, "end": v(9.86, 31) * mm});
            skLineSegment(sketch, "E854", {"start": v(9.86, 31) * mm, "end": v(9.8, 31.33) * mm});
            skLineSegment(sketch, "E855", {"start": v(9.8, 31.33) * mm, "end": v(9.71, 31.34) * mm});
            skLineSegment(sketch, "E856", {"start": v(9.71, 31.34) * mm, "end": v(9.6, 31.26) * mm});
            skLineSegment(sketch, "E857", {"start": v(9.6, 31.26) * mm, "end": v(9.4, 31.18) * mm});
            skLineSegment(sketch, "E858", {"start": v(9.4, 31.18) * mm, "end": v(9.18, 31.26) * mm});
            skLineSegment(sketch, "E859", {"start": v(9.18, 31.26) * mm, "end": v(9.14, 31.54) * mm});
            skLineSegment(sketch, "E860", {"start": v(9.14, 31.54) * mm, "end": v(9.1, 31.97) * mm});
            skLineSegment(sketch, "E861", {"start": v(9.1, 31.97) * mm, "end": v(9.1, 32.43) * mm});
            skLineSegment(sketch, "E862", {"start": v(9.1, 32.43) * mm, "end": v(9.07, 32.78) * mm});
            skLineSegment(sketch, "E863", {"start": v(9.07, 32.78) * mm, "end": v(8.85, 32.8) * mm});
            skLineSegment(sketch, "E864", {"start": v(8.85, 32.8) * mm, "end": v(8.69, 33.12) * mm});
            skLineSegment(sketch, "E865", {"start": v(8.69, 33.12) * mm, "end": v(8.61, 33.56) * mm});
            skLineSegment(sketch, "E866", {"start": v(8.61, 33.56) * mm, "end": v(8.49, 34.19) * mm});
            skLineSegment(sketch, "E867", {"start": v(8.49, 34.19) * mm, "end": v(8.48, 34.31) * mm});
            skLineSegment(sketch, "E868", {"start": v(8.48, 34.31) * mm, "end": v(8.28, 34.34) * mm});
            skLineSegment(sketch, "E869", {"start": v(8.28, 34.34) * mm, "end": v(8.14, 34.53) * mm});
            skLineSegment(sketch, "E870", {"start": v(8.14, 34.53) * mm, "end": v(8.07, 34.88) * mm});
            skLineSegment(sketch, "E871", {"start": v(8.07, 34.88) * mm, "end": v(8.05, 35.27) * mm});
            skLineSegment(sketch, "E872", {"start": v(8.05, 35.27) * mm, "end": v(7.96, 35.45) * mm});
            skLineSegment(sketch, "E873", {"start": v(7.96, 35.45) * mm, "end": v(7.82, 35.66) * mm});
            skLineSegment(sketch, "E874", {"start": v(7.82, 35.66) * mm, "end": v(7.6, 36.12) * mm});
            skLineSegment(sketch, "E875", {"start": v(7.6, 36.12) * mm, "end": v(7.41, 36.7) * mm});
            skLineSegment(sketch, "E876", {"start": v(7.41, 36.7) * mm, "end": v(7.15, 37.24) * mm});
            skLineSegment(sketch, "E877", {"start": v(7.15, 37.24) * mm, "end": v(6.88, 37.43) * mm});
            skLineSegment(sketch, "E878", {"start": v(6.88, 37.43) * mm, "end": v(6.55, 37.53) * mm});
            skLineSegment(sketch, "E879", {"start": v(6.55, 37.53) * mm, "end": v(6.35, 37.51) * mm});
            skLineSegment(sketch, "E880", {"start": v(6.35, 37.51) * mm, "end": v(6.18, 37.45) * mm});
            skLineSegment(sketch, "E881", {"start": v(6.18, 37.45) * mm, "end": v(6.07, 37.34) * mm});
            skLineSegment(sketch, "E882", {"start": v(6.07, 37.34) * mm, "end": v(5.93, 37.2) * mm});
            skLineSegment(sketch, "E883", {"start": v(5.93, 37.2) * mm, "end": v(5.78, 37.08) * mm});
            skLineSegment(sketch, "E884", {"start": v(5.78, 37.08) * mm, "end": v(5.6, 36.97) * mm});
            skLineSegment(sketch, "E885", {"start": v(5.6, 36.97) * mm, "end": v(5.42, 36.9) * mm});
            skLineSegment(sketch, "E886", {"start": v(5.42, 36.9) * mm, "end": v(5.1, 36.8) * mm});
            skLineSegment(sketch, "E887", {"start": v(5.1, 36.8) * mm, "end": v(4.78, 36.74) * mm});
            skLineSegment(sketch, "E888", {"start": v(4.78, 36.74) * mm, "end": v(4.5, 36.73) * mm});
            skLineSegment(sketch, "E889", {"start": v(4.5, 36.73) * mm, "end": v(4.09, 36.75) * mm});
            skLineSegment(sketch, "E890", {"start": v(4.09, 36.75) * mm, "end": v(3.79, 36.8) * mm});
            skLineSegment(sketch, "E891", {"start": v(3.79, 36.8) * mm, "end": v(3.5, 36.93) * mm});
            skLineSegment(sketch, "E892", {"start": v(3.5, 36.93) * mm, "end": v(3.2, 37.1) * mm});
            skLineSegment(sketch, "E893", {"start": v(3.2, 37.1) * mm, "end": v(2.92, 37.34) * mm});
            skLineSegment(sketch, "E894", {"start": v(2.92, 37.34) * mm, "end": v(2.72, 37.6) * mm});
            skLineSegment(sketch, "E895", {"start": v(2.72, 37.6) * mm, "end": v(2.56, 37.86) * mm});
            skLineSegment(sketch, "E896", {"start": v(2.56, 37.86) * mm, "end": v(2.52, 38.05) * mm});
            skLineSegment(sketch, "E897", {"start": v(2.52, 38.05) * mm, "end": v(2.5, 38.19) * mm});
            skLineSegment(sketch, "E898", {"start": v(2.5, 38.19) * mm, "end": v(2.57, 38.23) * mm});
            skLineSegment(sketch, "E899", {"start": v(2.57, 38.23) * mm, "end": v(2.7, 38.22) * mm});
            skLineSegment(sketch, "E900", {"start": v(2.7, 38.22) * mm, "end": v(2.88, 38.15) * mm});
            skLineSegment(sketch, "E901", {"start": v(2.88, 38.15) * mm, "end": v(3.22, 37.98) * mm});
            skLineSegment(sketch, "E902", {"start": v(3.22, 37.98) * mm, "end": v(3.72, 37.89) * mm});
            skLineSegment(sketch, "E903", {"start": v(3.72, 37.89) * mm, "end": v(4.04, 37.87) * mm});
            skLineSegment(sketch, "E904", {"start": v(4.04, 37.87) * mm, "end": v(4.32, 37.94) * mm});
            skLineSegment(sketch, "E905", {"start": v(4.32, 37.94) * mm, "end": v(4.47, 38) * mm});
            skLineSegment(sketch, "E906", {"start": v(4.47, 38) * mm, "end": v(4.55, 38.1) * mm});
            skLineSegment(sketch, "E907", {"start": v(4.55, 38.1) * mm, "end": v(4.55, 38.4) * mm});
            skLineSegment(sketch, "E908", {"start": v(4.55, 38.4) * mm, "end": v(4.57, 38.53) * mm});
            skLineSegment(sketch, "E909", {"start": v(4.57, 38.53) * mm, "end": v(4.68, 38.69) * mm});
            skLineSegment(sketch, "E910", {"start": v(4.68, 38.69) * mm, "end": v(4.86, 38.87) * mm});
            skLineSegment(sketch, "E911", {"start": v(4.86, 38.87) * mm, "end": v(5.06, 38.96) * mm});
            skLineSegment(sketch, "E912", {"start": v(5.06, 38.96) * mm, "end": v(5.24, 39.04) * mm});
            skLineSegment(sketch, "E913", {"start": v(5.24, 39.04) * mm, "end": v(5.56, 39.04) * mm});
            skLineSegment(sketch, "E914", {"start": v(5.56, 39.04) * mm, "end": v(5.87, 39) * mm});
            skLineSegment(sketch, "E915", {"start": v(5.87, 39) * mm, "end": v(6.07, 39.04) * mm});
            skLineSegment(sketch, "E916", {"start": v(6.07, 39.04) * mm, "end": v(6.14, 39.14) * mm});
            skLineSegment(sketch, "E917", {"start": v(6.14, 39.14) * mm, "end": v(6.02, 39.42) * mm});
            skLineSegment(sketch, "E918", {"start": v(6.02, 39.42) * mm, "end": v(5.86, 39.55) * mm});
            skLineSegment(sketch, "E919", {"start": v(5.86, 39.55) * mm, "end": v(5.68, 39.72) * mm});
            skLineSegment(sketch, "E920", {"start": v(5.68, 39.72) * mm, "end": v(5.5, 39.88) * mm});
            skLineSegment(sketch, "E921", {"start": v(5.5, 39.88) * mm, "end": v(5.37, 39.93) * mm});
            skLineSegment(sketch, "E922", {"start": v(5.37, 39.93) * mm, "end": v(5.19, 39.93) * mm});
            skLineSegment(sketch, "E923", {"start": v(5.19, 39.93) * mm, "end": v(4.98, 39.9) * mm});
            skLineSegment(sketch, "E924", {"start": v(4.98, 39.9) * mm, "end": v(4.7, 39.88) * mm});
            skLineSegment(sketch, "E925", {"start": v(4.7, 39.88) * mm, "end": v(4.47, 39.9) * mm});
            skLineSegment(sketch, "E926", {"start": v(4.47, 39.9) * mm, "end": v(4.32, 39.97) * mm});
            skLineSegment(sketch, "E927", {"start": v(4.32, 39.97) * mm, "end": v(3.94, 40.25) * mm});
            skLineSegment(sketch, "E928", {"start": v(3.94, 40.25) * mm, "end": v(3.71, 40.3) * mm});
            skLineSegment(sketch, "E929", {"start": v(3.71, 40.3) * mm, "end": v(3.36, 40.32) * mm});
            skLineSegment(sketch, "E930", {"start": v(3.36, 40.32) * mm, "end": v(3.02, 40.34) * mm});
            skLineSegment(sketch, "E931", {"start": v(3.02, 40.34) * mm, "end": v(2.75, 40.32) * mm});
            skLineSegment(sketch, "E932", {"start": v(2.75, 40.32) * mm, "end": v(2.46, 40.27) * mm});
            skLineSegment(sketch, "E933", {"start": v(2.46, 40.27) * mm, "end": v(2.28, 40.2) * mm});
            skLineSegment(sketch, "E934", {"start": v(2.28, 40.2) * mm, "end": v(2.17, 40.2) * mm});
            skLineSegment(sketch, "E935", {"start": v(2.17, 40.2) * mm, "end": v(2.1, 40.3) * mm});
            skLineSegment(sketch, "E936", {"start": v(2.1, 40.3) * mm, "end": v(2.21, 40.56) * mm});
            skLineSegment(sketch, "E937", {"start": v(2.21, 40.56) * mm, "end": v(2.38, 40.82) * mm});
            skLineSegment(sketch, "E938", {"start": v(2.38, 40.82) * mm, "end": v(2.62, 41.08) * mm});
            skLineSegment(sketch, "E939", {"start": v(2.62, 41.08) * mm, "end": v(2.92, 41.28) * mm});
            skLineSegment(sketch, "E940", {"start": v(2.92, 41.28) * mm, "end": v(3.24, 41.43) * mm});
            skLineSegment(sketch, "E941", {"start": v(3.24, 41.43) * mm, "end": v(3.59, 41.51) * mm});
            skLineSegment(sketch, "E942", {"start": v(3.59, 41.51) * mm, "end": v(3.96, 41.54) * mm});
            skLineSegment(sketch, "E943", {"start": v(3.96, 41.54) * mm, "end": v(4.23, 41.6) * mm});
            skLineSegment(sketch, "E944", {"start": v(4.23, 41.6) * mm, "end": v(4.46, 41.68) * mm});
            skLineSegment(sketch, "E945", {"start": v(4.46, 41.68) * mm, "end": v(4.77, 41.7) * mm});
            skLineSegment(sketch, "E946", {"start": v(4.77, 41.7) * mm, "end": v(5.06, 41.65) * mm});
            skLineSegment(sketch, "E947", {"start": v(5.06, 41.65) * mm, "end": v(5.05, 41.77) * mm});
            skLineSegment(sketch, "E948", {"start": v(5.05, 41.77) * mm, "end": v(4.92, 41.9) * mm});
            skLineSegment(sketch, "E949", {"start": v(4.92, 41.9) * mm, "end": v(4.7, 42.03) * mm});
            skLineSegment(sketch, "E950", {"start": v(4.7, 42.03) * mm, "end": v(4.6, 42.14) * mm});
            skLineSegment(sketch, "E951", {"start": v(4.6, 42.14) * mm, "end": v(4.3, 42.2) * mm});
            skLineSegment(sketch, "E952", {"start": v(4.3, 42.2) * mm, "end": v(4.16, 42.25) * mm});
            skLineSegment(sketch, "E953", {"start": v(4.16, 42.25) * mm, "end": v(3.91, 42.23) * mm});
            skLineSegment(sketch, "E954", {"start": v(3.91, 42.23) * mm, "end": v(3.68, 42.23) * mm});
            skLineSegment(sketch, "E955", {"start": v(3.68, 42.23) * mm, "end": v(3.5, 42.3) * mm});
            skLineSegment(sketch, "E956", {"start": v(3.5, 42.3) * mm, "end": v(3.46, 42.52) * mm});
            skLineSegment(sketch, "E957", {"start": v(3.46, 42.52) * mm, "end": v(3.57, 42.67) * mm});
            skLineSegment(sketch, "E958", {"start": v(3.57, 42.67) * mm, "end": v(3.87, 42.85) * mm});
            skLineSegment(sketch, "E959", {"start": v(3.87, 42.85) * mm, "end": v(4.25, 43.01) * mm});
            skLineSegment(sketch, "E960", {"start": v(4.25, 43.01) * mm, "end": v(4.8, 43.1) * mm});
            skLineSegment(sketch, "E961", {"start": v(4.8, 43.1) * mm, "end": v(5.48, 42.96) * mm});
            skLineSegment(sketch, "E962", {"start": v(5.48, 42.96) * mm, "end": v(6, 42.74) * mm});
            skLineSegment(sketch, "E963", {"start": v(6, 42.74) * mm, "end": v(6.4, 42.5) * mm});
            skLineSegment(sketch, "E964", {"start": v(6.4, 42.5) * mm, "end": v(6.71, 42.22) * mm});
            skLineSegment(sketch, "E965", {"start": v(6.71, 42.22) * mm, "end": v(6.84, 42.1) * mm});
            skLineSegment(sketch, "E966", {"start": v(6.84, 42.1) * mm, "end": v(6.9, 42.03) * mm});
            skLineSegment(sketch, "E967", {"start": v(6.9, 42.03) * mm, "end": v(6.98, 42.06) * mm});
            skLineSegment(sketch, "E968", {"start": v(6.98, 42.06) * mm, "end": v(7.08, 42.15) * mm});
            skLineSegment(sketch, "E969", {"start": v(7.08, 42.15) * mm, "end": v(7.22, 42.24) * mm});
            skLineSegment(sketch, "E970", {"start": v(7.22, 42.24) * mm, "end": v(7.3, 42.34) * mm});
            skLineSegment(sketch, "E971", {"start": v(7.3, 42.34) * mm, "end": v(7.28, 42.57) * mm});
            skLineSegment(sketch, "E972", {"start": v(7.28, 42.57) * mm, "end": v(7.17, 42.73) * mm});
            skLineSegment(sketch, "E973", {"start": v(7.17, 42.73) * mm, "end": v(7.05, 42.98) * mm});
            skLineSegment(sketch, "E974", {"start": v(7.05, 42.98) * mm, "end": v(6.91, 43.19) * mm});
            skLineSegment(sketch, "E975", {"start": v(6.91, 43.19) * mm, "end": v(6.66, 43.45) * mm});
            skLineSegment(sketch, "E976", {"start": v(6.66, 43.45) * mm, "end": v(6.42, 43.63) * mm});
            skLineSegment(sketch, "E977", {"start": v(6.42, 43.63) * mm, "end": v(6.28, 43.8) * mm});
            skLineSegment(sketch, "E978", {"start": v(6.28, 43.8) * mm, "end": v(6.26, 43.86) * mm});
            skLineSegment(sketch, "E979", {"start": v(6.26, 43.86) * mm, "end": v(6.32, 43.92) * mm});
            skLineSegment(sketch, "E980", {"start": v(6.32, 43.92) * mm, "end": v(6.55, 43.97) * mm});
            skLineSegment(sketch, "E981", {"start": v(6.55, 43.97) * mm, "end": v(6.9, 43.96) * mm});
            skLineSegment(sketch, "E982", {"start": v(6.9, 43.96) * mm, "end": v(7.2, 43.87) * mm});
            skLineSegment(sketch, "E983", {"start": v(7.2, 43.87) * mm, "end": v(7.47, 43.78) * mm});
            skLineSegment(sketch, "E984", {"start": v(7.47, 43.78) * mm, "end": v(7.68, 43.6) * mm});
            skLineSegment(sketch, "E985", {"start": v(7.68, 43.6) * mm, "end": v(7.96, 43.4) * mm});
            skLineSegment(sketch, "E986", {"start": v(7.96, 43.4) * mm, "end": v(8.15, 43.22) * mm});
            skLineSegment(sketch, "E987", {"start": v(8.15, 43.22) * mm, "end": v(8.32, 42.98) * mm});
            skLineSegment(sketch, "E988", {"start": v(8.32, 42.98) * mm, "end": v(8.35, 42.8) * mm});
            skLineSegment(sketch, "E989", {"start": v(8.35, 42.8) * mm, "end": v(8.48, 42.65) * mm});
            skLineSegment(sketch, "E990", {"start": v(8.48, 42.65) * mm, "end": v(8.68, 42.5) * mm});
            skLineSegment(sketch, "E991", {"start": v(8.68, 42.5) * mm, "end": v(8.8, 42.3) * mm});
            skLineSegment(sketch, "E992", {"start": v(8.8, 42.3) * mm, "end": v(8.85, 42.15) * mm});
            skLineSegment(sketch, "E993", {"start": v(8.85, 42.15) * mm, "end": v(8.9, 41.89) * mm});
            skLineSegment(sketch, "E994", {"start": v(8.9, 41.89) * mm, "end": v(8.85, 41.7) * mm});
            skLineSegment(sketch, "E995", {"start": v(8.85, 41.7) * mm, "end": v(8.84, 41.55) * mm});
            skLineSegment(sketch, "E996", {"start": v(8.84, 41.55) * mm, "end": v(8.74, 41.12) * mm});
            skLineSegment(sketch, "E997", {"start": v(8.74, 41.12) * mm, "end": v(8.68, 40.8) * mm});
            skLineSegment(sketch, "E998", {"start": v(8.68, 40.8) * mm, "end": v(8.65, 40.52) * mm});
            skLineSegment(sketch, "E999", {"start": v(8.65, 40.52) * mm, "end": v(8.65, 40.3) * mm});
            skLineSegment(sketch, "E1000", {"start": v(8.65, 40.3) * mm, "end": v(8.72, 40.07) * mm});
            skLineSegment(sketch, "E1001", {"start": v(8.72, 40.07) * mm, "end": v(8.82, 39.9) * mm});
            skLineSegment(sketch, "E1002", {"start": v(8.82, 39.9) * mm, "end": v(9.12, 39.61) * mm});
            skLineSegment(sketch, "E1003", {"start": v(9.12, 39.61) * mm, "end": v(9.47, 39.2) * mm});
            skLineSegment(sketch, "E1004", {"start": v(9.47, 39.2) * mm, "end": v(9.85, 38.98) * mm});
            skLineSegment(sketch, "E1005", {"start": v(9.85, 38.98) * mm, "end": v(10.35, 38.56) * mm});
            skLineSegment(sketch, "E1006", {"start": v(10.35, 38.56) * mm, "end": v(10.75, 38.18) * mm});
            skLineSegment(sketch, "E1007", {"start": v(10.75, 38.18) * mm, "end": v(11.11, 37.8) * mm});
            skLineSegment(sketch, "E1008", {"start": v(11.11, 37.8) * mm, "end": v(11.5, 37.4) * mm});
            skLineSegment(sketch, "E1009", {"start": v(11.5, 37.4) * mm, "end": v(11.83, 36.95) * mm});
            skLineSegment(sketch, "E1010", {"start": v(11.83, 36.95) * mm, "end": v(12.21, 36.23) * mm});
            skLineSegment(sketch, "E1011", {"start": v(12.21, 36.23) * mm, "end": v(12.5, 35.74) * mm});
            skLineSegment(sketch, "E1012", {"start": v(12.5, 35.74) * mm, "end": v(13.08, 34.98) * mm});
            skLineSegment(sketch, "E1013", {"start": v(13.08, 34.98) * mm, "end": v(13.37, 34.36) * mm});
            skLineSegment(sketch, "E1014", {"start": v(13.37, 34.36) * mm, "end": v(13.8, 33.64) * mm});
            skLineSegment(sketch, "E1015", {"start": v(13.8, 33.64) * mm, "end": v(14.16, 33.2) * mm});
            skLineSegment(sketch, "E1016", {"start": v(14.16, 33.2) * mm, "end": v(14.75, 32.58) * mm});
            skLineSegment(sketch, "E1017", {"start": v(14.75, 32.58) * mm, "end": v(15.16, 32.18) * mm});
            skLineSegment(sketch, "E1018", {"start": v(15.16, 32.18) * mm, "end": v(15.64, 31.86) * mm});
            skLineSegment(sketch, "E1019", {"start": v(15.64, 31.86) * mm, "end": v(15.94, 31.63) * mm});
            skLineSegment(sketch, "E1020", {"start": v(15.94, 31.63) * mm, "end": v(16.08, 31.62) * mm});
            skLineSegment(sketch, "E1021", {"start": v(16.08, 31.62) * mm, "end": v(16.34, 31.66) * mm});
            skLineSegment(sketch, "E1022", {"start": v(16.34, 31.66) * mm, "end": v(17.33, 31.9) * mm});
            skLineSegment(sketch, "E1023", {"start": v(17.33, 31.9) * mm, "end": v(18.14, 32.11) * mm});
            skLineSegment(sketch, "E1024", {"start": v(18.14, 32.11) * mm, "end": v(18.65, 32.25) * mm});
            skLineSegment(sketch, "E1025", {"start": v(18.65, 32.25) * mm, "end": v(19.1, 32.3) * mm});
            skLineSegment(sketch, "E1026", {"start": v(19.1, 32.3) * mm, "end": v(19.52, 32.34) * mm});
            skLineSegment(sketch, "E1027", {"start": v(19.52, 32.34) * mm, "end": v(19.79, 32.38) * mm});
            skLineSegment(sketch, "E1028", {"start": v(19.79, 32.38) * mm, "end": v(20.14, 32.47) * mm});
            skLineSegment(sketch, "E1029", {"start": v(20.14, 32.47) * mm, "end": v(20.55, 32.8) * mm});
            skLineSegment(sketch, "E1030", {"start": v(20.55, 32.8) * mm, "end": v(20.65, 32.96) * mm});
            skLineSegment(sketch, "E1031", {"start": v(20.65, 32.96) * mm, "end": v(20.68, 33.14) * mm});
            skLineSegment(sketch, "E1032", {"start": v(20.68, 33.14) * mm, "end": v(20.65, 33.18) * mm});
            skLineSegment(sketch, "E1033", {"start": v(20.65, 33.18) * mm, "end": v(18.08, 33.2) * mm});
            skLineSegment(sketch, "E1034", {"start": v(18.08, 33.2) * mm, "end": v(17.9, 33.1) * mm});
            skLineSegment(sketch, "E1035", {"start": v(17.9, 33.1) * mm, "end": v(17.56, 32.94) * mm});
            skLineSegment(sketch, "E1036", {"start": v(17.56, 32.94) * mm, "end": v(17.39, 32.84) * mm});
            skLineSegment(sketch, "E1037", {"start": v(17.39, 32.84) * mm, "end": v(17.13, 32.82) * mm});
            skLineSegment(sketch, "E1038", {"start": v(17.13, 32.82) * mm, "end": v(16.76, 32.81) * mm});
            skLineSegment(sketch, "E1039", {"start": v(16.76, 32.81) * mm, "end": v(16.59, 32.83) * mm});
            skLineSegment(sketch, "E1040", {"start": v(16.59, 32.83) * mm, "end": v(16.45, 32.97) * mm});
            skLineSegment(sketch, "E1041", {"start": v(16.45, 32.97) * mm, "end": v(16.54, 33.1) * mm});
            skLineSegment(sketch, "E1042", {"start": v(16.54, 33.1) * mm, "end": v(16.75, 33.25) * mm});
            skLineSegment(sketch, "E1043", {"start": v(16.75, 33.25) * mm, "end": v(16.94, 33.43) * mm});
            skLineSegment(sketch, "E1044", {"start": v(16.94, 33.43) * mm, "end": v(17.05, 33.87) * mm});
            skLineSegment(sketch, "E1045", {"start": v(17.05, 33.87) * mm, "end": v(17.07, 34.18) * mm});
            skLineSegment(sketch, "E1046", {"start": v(17.07, 34.18) * mm, "end": v(17.06, 34.41) * mm});
            skLineSegment(sketch, "E1047", {"start": v(17.06, 34.41) * mm, "end": v(17.13, 34.55) * mm});
            skLineSegment(sketch, "E1048", {"start": v(17.13, 34.55) * mm, "end": v(17.32, 34.54) * mm});
            skLineSegment(sketch, "E1049", {"start": v(17.32, 34.54) * mm, "end": v(17.53, 34.54) * mm});
            skLineSegment(sketch, "E1050", {"start": v(17.53, 34.54) * mm, "end": v(17.98, 35) * mm});
            skLineSegment(sketch, "E1051", {"start": v(17.98, 35) * mm, "end": v(18.56, 34.53) * mm});
            skLineSegment(sketch, "E1052", {"start": v(18.56, 34.53) * mm, "end": v(20.33, 34.54) * mm});
            skLineSegment(sketch, "E1053", {"start": v(20.33, 34.54) * mm, "end": v(20.6, 34.68) * mm});
            skLineSegment(sketch, "E1054", {"start": v(20.6, 34.68) * mm, "end": v(20.66, 34.85) * mm});
            skLineSegment(sketch, "E1055", {"start": v(20.66, 34.85) * mm, "end": v(20.7, 35.15) * mm});
            skLineSegment(sketch, "E1056", {"start": v(20.7, 35.15) * mm, "end": v(20.6, 35.26) * mm});
            skLineSegment(sketch, "E1057", {"start": v(20.6, 35.26) * mm, "end": v(20.4, 35.29) * mm});
            skLineSegment(sketch, "E1058", {"start": v(20.4, 35.29) * mm, "end": v(16.6, 35.28) * mm});
            skLineSegment(sketch, "E1059", {"start": v(16.6, 35.28) * mm, "end": v(16.05, 35.5) * mm});
            skLineSegment(sketch, "E1060", {"start": v(16.05, 35.5) * mm, "end": v(15.66, 35.8) * mm});
            skLineSegment(sketch, "E1061", {"start": v(15.66, 35.8) * mm, "end": v(15.38, 36.14) * mm});
            skLineSegment(sketch, "E1062", {"start": v(15.38, 36.14) * mm, "end": v(15.2, 36.57) * mm});
            skLineSegment(sketch, "E1063", {"start": v(15.2, 36.57) * mm, "end": v(15.07, 37.02) * mm});
            skLineSegment(sketch, "E1064", {"start": v(15.07, 37.02) * mm, "end": v(15.07, 37.35) * mm});
            skLineSegment(sketch, "E1065", {"start": v(15.07, 37.35) * mm, "end": v(15.11, 37.74) * mm});
            skLineSegment(sketch, "E1066", {"start": v(15.11, 37.74) * mm, "end": v(15.2, 37.98) * mm});
            skLineSegment(sketch, "E1067", {"start": v(15.2, 37.98) * mm, "end": v(15.34, 38.12) * mm});
            skLineSegment(sketch, "E1068", {"start": v(15.34, 38.12) * mm, "end": v(15.58, 37.88) * mm});
            skLineSegment(sketch, "E1069", {"start": v(15.58, 37.88) * mm, "end": v(15.7, 37.4) * mm});
            skLineSegment(sketch, "E1070", {"start": v(15.7, 37.4) * mm, "end": v(15.85, 36.95) * mm});
            skLineSegment(sketch, "E1071", {"start": v(15.85, 36.95) * mm, "end": v(16, 36.64) * mm});
            skLineSegment(sketch, "E1072", {"start": v(16, 36.64) * mm, "end": v(16.2, 36.44) * mm});
            skLineSegment(sketch, "E1073", {"start": v(16.2, 36.44) * mm, "end": v(16.68, 35.97) * mm});
            skLineSegment(sketch, "E1074", {"start": v(16.68, 35.97) * mm, "end": v(16.91, 35.86) * mm});
            skLineSegment(sketch, "E1075", {"start": v(16.91, 35.86) * mm, "end": v(17.48, 35.86) * mm});
            skLineSegment(sketch, "E1076", {"start": v(17.48, 35.86) * mm, "end": v(20.42, 35.9) * mm});
            skLineSegment(sketch, "E1077", {"start": v(20.42, 35.9) * mm, "end": v(20.5, 36.04) * mm});
            skLineSegment(sketch, "E1078", {"start": v(20.5, 36.04) * mm, "end": v(20.42, 36.68) * mm});
            skLineSegment(sketch, "E1079", {"start": v(20.42, 36.68) * mm, "end": v(20.4, 37) * mm});
            skLineSegment(sketch, "E1080", {"start": v(20.4, 37) * mm, "end": v(20.34, 37.16) * mm});
            skLineSegment(sketch, "E1081", {"start": v(20.34, 37.16) * mm, "end": v(19.88, 37.24) * mm});
            skLineSegment(sketch, "E1082", {"start": v(19.88, 37.24) * mm, "end": v(19.4, 37.28) * mm});
            skLineSegment(sketch, "E1083", {"start": v(19.4, 37.28) * mm, "end": v(19, 37.19) * mm});
            skLineSegment(sketch, "E1084", {"start": v(19, 37.19) * mm, "end": v(18.68, 37.08) * mm});
            skLineSegment(sketch, "E1085", {"start": v(18.68, 37.08) * mm, "end": v(18.48, 36.91) * mm});
            skLineSegment(sketch, "E1086", {"start": v(18.48, 36.91) * mm, "end": v(18.06, 36.22) * mm});
            skLineSegment(sketch, "E1087", {"start": v(18.06, 36.22) * mm, "end": v(17.45, 36.96) * mm});
            skLineSegment(sketch, "E1088", {"start": v(17.45, 36.96) * mm, "end": v(17.12, 37.11) * mm});
            skLineSegment(sketch, "E1089", {"start": v(17.12, 37.11) * mm, "end": v(16.83, 37.32) * mm});
            skLineSegment(sketch, "E1090", {"start": v(16.83, 37.32) * mm, "end": v(16.62, 37.55) * mm});
            skLineSegment(sketch, "E1091", {"start": v(16.62, 37.55) * mm, "end": v(16.6, 37.86) * mm});
            skLineSegment(sketch, "E1092", {"start": v(16.6, 37.86) * mm, "end": v(16.62, 38.13) * mm});
            skLineSegment(sketch, "E1093", {"start": v(16.62, 38.13) * mm, "end": v(16.66, 38.46) * mm});
            skLineSegment(sketch, "E1094", {"start": v(16.66, 38.46) * mm, "end": v(16.7, 38.72) * mm});
            skLineSegment(sketch, "E1095", {"start": v(16.7, 38.72) * mm, "end": v(16.4, 39.32) * mm});
            skLineSegment(sketch, "E1096", {"start": v(16.4, 39.32) * mm, "end": v(16.46, 39.58) * mm});
            skLineSegment(sketch, "E1097", {"start": v(16.46, 39.58) * mm, "end": v(16.6, 39.79) * mm});
            skLineSegment(sketch, "E1098", {"start": v(16.6, 39.79) * mm, "end": v(16.83, 39.83) * mm});
            skLineSegment(sketch, "E1099", {"start": v(16.83, 39.83) * mm, "end": v(17.28, 39.8) * mm});
            skLineSegment(sketch, "E1100", {"start": v(17.28, 39.8) * mm, "end": v(17.74, 39.82) * mm});
            skLineSegment(sketch, "E1101", {"start": v(17.74, 39.82) * mm, "end": v(18.36, 39.9) * mm});
            skLineSegment(sketch, "E1102", {"start": v(18.36, 39.9) * mm, "end": v(18.82, 40.05) * mm});
            skLineSegment(sketch, "E1103", {"start": v(18.82, 40.05) * mm, "end": v(19.3, 40.21) * mm});
            skLineSegment(sketch, "E1104", {"start": v(19.3, 40.21) * mm, "end": v(19.6, 40.38) * mm});
            skLineSegment(sketch, "E1105", {"start": v(19.6, 40.38) * mm, "end": v(19.97, 40.53) * mm});
            skLineSegment(sketch, "E1106", {"start": v(19.97, 40.53) * mm, "end": v(20.12, 40.63) * mm});
            skLineSegment(sketch, "E1107", {"start": v(20.12, 40.63) * mm, "end": v(20.6, 40.64) * mm});
            skLineSegment(sketch, "E1108", {"start": v(20.6, 40.64) * mm, "end": v(21.64, 40.72) * mm});
            skLineSegment(sketch, "E1109", {"start": v(21.64, 40.72) * mm, "end": v(22.97, 41.84) * mm});
            skLineSegment(sketch, "E1110", {"start": v(22.97, 41.84) * mm, "end": v(23.22, 41.59) * mm});
            skLineSegment(sketch, "E1111", {"start": v(23.22, 41.59) * mm, "end": v(23.14, 40.75) * mm});
            skLineSegment(sketch, "E1112", {"start": v(23.14, 40.75) * mm, "end": v(23.52, 40.58) * mm});
            skLineSegment(sketch, "E1113", {"start": v(23.52, 40.58) * mm, "end": v(24.05, 40.3) * mm});
            skLineSegment(sketch, "E1114", {"start": v(24.05, 40.3) * mm, "end": v(24.38, 40.05) * mm});
            skLineSegment(sketch, "E1115", {"start": v(24.38, 40.05) * mm, "end": v(24.71, 39.67) * mm});
            skLineSegment(sketch, "E1116", {"start": v(24.71, 39.67) * mm, "end": v(24.92, 39.36) * mm});
            skLineSegment(sketch, "E1117", {"start": v(24.92, 39.36) * mm, "end": v(25.11, 39.13) * mm});
            skLineSegment(sketch, "E1118", {"start": v(25.11, 39.13) * mm, "end": v(25.22, 39) * mm});
            skLineSegment(sketch, "E1119", {"start": v(25.22, 39) * mm, "end": v(25.51, 38.95) * mm});
            skLineSegment(sketch, "E1120", {"start": v(25.51, 38.95) * mm, "end": v(25.74, 39) * mm});
            skLineSegment(sketch, "E1121", {"start": v(25.74, 39) * mm, "end": v(25.87, 39.04) * mm});
            skLineSegment(sketch, "E1122", {"start": v(25.87, 39.04) * mm, "end": v(26, 39.1) * mm});
            skLineSegment(sketch, "E1123", {"start": v(26, 39.1) * mm, "end": v(26.19, 39.27) * mm});
            skLineSegment(sketch, "E1124", {"start": v(26.19, 39.27) * mm, "end": v(26.34, 39.37) * mm});
            skLineSegment(sketch, "E1125", {"start": v(26.34, 39.37) * mm, "end": v(26.5, 39.22) * mm});
            skLineSegment(sketch, "E1126", {"start": v(26.5, 39.22) * mm, "end": v(26.5, 39.07) * mm});
            skLineSegment(sketch, "E1127", {"start": v(26.5, 39.07) * mm, "end": v(26.4, 38.86) * mm});
            skLineSegment(sketch, "E1128", {"start": v(26.4, 38.86) * mm, "end": v(26.32, 38.72) * mm});
            skLineSegment(sketch, "E1129", {"start": v(26.32, 38.72) * mm, "end": v(26.3, 38.52) * mm});
            skLineSegment(sketch, "E1130", {"start": v(26.3, 38.52) * mm, "end": v(26.27, 38.27) * mm});
            skLineSegment(sketch, "E1131", {"start": v(26.27, 38.27) * mm, "end": v(26.31, 37.91) * mm});
            skLineSegment(sketch, "E1132", {"start": v(26.31, 37.91) * mm, "end": v(26.38, 37.54) * mm});
            skLineSegment(sketch, "E1133", {"start": v(26.38, 37.54) * mm, "end": v(26.47, 37.17) * mm});
            skLineSegment(sketch, "E1134", {"start": v(26.47, 37.17) * mm, "end": v(26.49, 36.86) * mm});
            skLineSegment(sketch, "E1135", {"start": v(26.49, 36.86) * mm, "end": v(26.48, 36.54) * mm});
            skLineSegment(sketch, "E1136", {"start": v(26.48, 36.54) * mm, "end": v(26.53, 36.29) * mm});
            skLineSegment(sketch, "E1137", {"start": v(26.53, 36.29) * mm, "end": v(26.51, 36.18) * mm});
            skLineSegment(sketch, "E1138", {"start": v(26.51, 36.18) * mm, "end": v(26.62, 35.95) * mm});
            skLineSegment(sketch, "E1139", {"start": v(26.62, 35.95) * mm, "end": v(26.96, 35.7) * mm});
            skLineSegment(sketch, "E1140", {"start": v(26.96, 35.7) * mm, "end": v(27.4, 35.48) * mm});
            skLineSegment(sketch, "E1141", {"start": v(27.4, 35.48) * mm, "end": v(27.9, 35.28) * mm});
            skLineSegment(sketch, "E1142", {"start": v(27.9, 35.28) * mm, "end": v(28.09, 35.17) * mm});
            skLineSegment(sketch, "E1143", {"start": v(28.09, 35.17) * mm, "end": v(28.1, 34.96) * mm});
            skLineSegment(sketch, "E1144", {"start": v(28.1, 34.96) * mm, "end": v(27.95, 34.74) * mm});
            skLineSegment(sketch, "E1145", {"start": v(27.95, 34.74) * mm, "end": v(27.73, 34.61) * mm});
            skLineSegment(sketch, "E1146", {"start": v(27.73, 34.61) * mm, "end": v(27.5, 34.54) * mm});
            skLineSegment(sketch, "E1147", {"start": v(27.5, 34.54) * mm, "end": v(27.2, 34.53) * mm});
            skLineSegment(sketch, "E1148", {"start": v(27.2, 34.53) * mm, "end": v(26.75, 34.52) * mm});
            skLineSegment(sketch, "E1149", {"start": v(26.75, 34.52) * mm, "end": v(26.67, 34.44) * mm});
            skLineSegment(sketch, "E1150", {"start": v(26.67, 34.44) * mm, "end": v(26.7, 34.31) * mm});
            skLineSegment(sketch, "E1151", {"start": v(26.7, 34.31) * mm, "end": v(26.74, 34.07) * mm});
            skLineSegment(sketch, "E1152", {"start": v(26.74, 34.07) * mm, "end": v(26.8, 33.77) * mm});
            skLineSegment(sketch, "E1153", {"start": v(26.8, 33.77) * mm, "end": v(27, 33.42) * mm});
            skLineSegment(sketch, "E1154", {"start": v(27, 33.42) * mm, "end": v(27.14, 33.08) * mm});
            skLineSegment(sketch, "E1155", {"start": v(27.14, 33.08) * mm, "end": v(27.4, 32.74) * mm});
            skLineSegment(sketch, "E1156", {"start": v(27.4, 32.74) * mm, "end": v(27.82, 32.47) * mm});
            skLineSegment(sketch, "E1157", {"start": v(27.82, 32.47) * mm, "end": v(28.07, 32.32) * mm});
            skLineSegment(sketch, "E1158", {"start": v(28.07, 32.32) * mm, "end": v(28.15, 32.13) * mm});
            skLineSegment(sketch, "E1159", {"start": v(28.15, 32.13) * mm, "end": v(28.04, 31.94) * mm});
            skLineSegment(sketch, "E1160", {"start": v(28.04, 31.94) * mm, "end": v(27.88, 31.83) * mm});
            skLineSegment(sketch, "E1161", {"start": v(27.88, 31.83) * mm, "end": v(27.78, 31.75) * mm});
            skLineSegment(sketch, "E1162", {"start": v(27.78, 31.75) * mm, "end": v(27.6, 31.64) * mm});
            skLineSegment(sketch, "E1163", {"start": v(27.6, 31.64) * mm, "end": v(27.37, 31.62) * mm});
            skLineSegment(sketch, "E1164", {"start": v(27.37, 31.62) * mm, "end": v(26.76, 31.62) * mm});
            skLineSegment(sketch, "E1165", {"start": v(26.76, 31.62) * mm, "end": v(26.7, 31.34) * mm});
            skLineSegment(sketch, "E1166", {"start": v(26.7, 31.34) * mm, "end": v(26.64, 31.1) * mm});
            skLineSegment(sketch, "E1167", {"start": v(26.64, 31.1) * mm, "end": v(26.7, 30.8) * mm});
            skLineSegment(sketch, "E1168", {"start": v(26.7, 30.8) * mm, "end": v(26.8, 30.47) * mm});
            skLineSegment(sketch, "E1169", {"start": v(26.8, 30.47) * mm, "end": v(26.94, 30.21) * mm});
            skLineSegment(sketch, "E1170", {"start": v(26.94, 30.21) * mm, "end": v(27.12, 29.96) * mm});
            skLineSegment(sketch, "E1171", {"start": v(27.12, 29.96) * mm, "end": v(27.37, 29.7) * mm});
            skLineSegment(sketch, "E1172", {"start": v(27.37, 29.7) * mm, "end": v(27.53, 29.54) * mm});
            skLineSegment(sketch, "E1173", {"start": v(27.53, 29.54) * mm, "end": v(27.66, 29.4) * mm});
            skLineSegment(sketch, "E1174", {"start": v(27.66, 29.4) * mm, "end": v(27.53, 29.15) * mm});
            skLineSegment(sketch, "E1175", {"start": v(27.53, 29.15) * mm, "end": v(27.33, 28.93) * mm});
            skLineSegment(sketch, "E1176", {"start": v(27.33, 28.93) * mm, "end": v(27.09, 28.82) * mm});
            skLineSegment(sketch, "E1177", {"start": v(27.09, 28.82) * mm, "end": v(26.77, 28.74) * mm});
            skLineSegment(sketch, "E1178", {"start": v(26.77, 28.74) * mm, "end": v(26.48, 28.8) * mm});
            skLineSegment(sketch, "E1179", {"start": v(26.48, 28.8) * mm, "end": v(26.32, 28.85) * mm});
            skLineSegment(sketch, "E1180", {"start": v(26.32, 28.85) * mm, "end": v(26.23, 28.56) * mm});
            skLineSegment(sketch, "E1181", {"start": v(26.23, 28.56) * mm, "end": v(26.3, 28.33) * mm});
            skLineSegment(sketch, "E1182", {"start": v(26.3, 28.33) * mm, "end": v(26.4, 28.03) * mm});
            skLineSegment(sketch, "E1183", {"start": v(26.4, 28.03) * mm, "end": v(26.54, 27.84) * mm});
            skLineSegment(sketch, "E1184", {"start": v(26.54, 27.84) * mm, "end": v(26.65, 27.68) * mm});
            skLineSegment(sketch, "E1185", {"start": v(26.65, 27.68) * mm, "end": v(26.9, 27.59) * mm});
            skLineSegment(sketch, "E1186", {"start": v(26.9, 27.59) * mm, "end": v(26.97, 27.43) * mm});
            skLineSegment(sketch, "E1187", {"start": v(26.97, 27.43) * mm, "end": v(26.92, 27.23) * mm});
            skLineSegment(sketch, "E1188", {"start": v(26.92, 27.23) * mm, "end": v(26.73, 27.07) * mm});
            skLineSegment(sketch, "E1189", {"start": v(26.73, 27.07) * mm, "end": v(26.3, 27.01) * mm});
            skLineSegment(sketch, "E1190", {"start": v(26.3, 27.01) * mm, "end": v(25.88, 27.07) * mm});
            skLineSegment(sketch, "E1191", {"start": v(25.88, 27.07) * mm, "end": v(25.47, 27.24) * mm});
            skLineSegment(sketch, "E1192", {"start": v(25.47, 27.24) * mm, "end": v(24.96, 27.93) * mm});
            skLineSegment(sketch, "E1193", {"start": v(24.96, 27.93) * mm, "end": v(24.74, 28.12) * mm});
            skLineSegment(sketch, "E1194", {"start": v(24.74, 28.12) * mm, "end": v(24.65, 27.78) * mm});
            skLineSegment(sketch, "E1195", {"start": v(24.65, 27.78) * mm, "end": v(24.82, 27.22) * mm});
            skLineSegment(sketch, "E1196", {"start": v(24.82, 27.22) * mm, "end": v(24.92, 26.6) * mm});
            skLineSegment(sketch, "E1197", {"start": v(24.92, 26.6) * mm, "end": v(25.15, 26.17) * mm});
            skLineSegment(sketch, "E1198", {"start": v(25.15, 26.17) * mm, "end": v(25.4, 25.72) * mm});
            skLineSegment(sketch, "E1199", {"start": v(25.4, 25.72) * mm, "end": v(25.65, 25.35) * mm});
            skLineSegment(sketch, "E1200", {"start": v(25.65, 25.35) * mm, "end": v(25.96, 24.82) * mm});
            skLineSegment(sketch, "E1201", {"start": v(25.96, 24.82) * mm, "end": v(26.4, 24.3) * mm});
            skLineSegment(sketch, "E1202", {"start": v(26.4, 24.3) * mm, "end": v(26.83, 23.79) * mm});
            skLineSegment(sketch, "E1203", {"start": v(26.83, 23.79) * mm, "end": v(27.24, 23.03) * mm});
            skLineSegment(sketch, "E1204", {"start": v(27.24, 23.03) * mm, "end": v(27.53, 22.3) * mm});
            skLineSegment(sketch, "E1205", {"start": v(27.53, 22.3) * mm, "end": v(27.95, 21.58) * mm});
            skLineSegment(sketch, "E1206", {"start": v(27.95, 21.58) * mm, "end": v(28.48, 20.75) * mm});
            skLineSegment(sketch, "E1207", {"start": v(28.48, 20.75) * mm, "end": v(29.14, 19.94) * mm});
            skLineSegment(sketch, "E1208", {"start": v(29.14, 19.94) * mm, "end": v(29.8, 19.5) * mm});
            skLineSegment(sketch, "E1209", {"start": v(29.8, 19.5) * mm, "end": v(30.58, 19.23) * mm});
            skLineSegment(sketch, "E1210", {"start": v(30.58, 19.23) * mm, "end": v(31.22, 19.09) * mm});
            skLineSegment(sketch, "E1211", {"start": v(31.22, 19.09) * mm, "end": v(31.96, 18.98) * mm});
            skLineSegment(sketch, "E1212", {"start": v(31.96, 18.98) * mm, "end": v(32.59, 19) * mm});
            skLineSegment(sketch, "E1213", {"start": v(32.59, 19) * mm, "end": v(33.4, 19.1) * mm});
            skLineSegment(sketch, "E1214", {"start": v(33.4, 19.1) * mm, "end": v(34.5, 19.69) * mm});
            skLineSegment(sketch, "E1215", {"start": v(34.5, 19.69) * mm, "end": v(34.95, 20.17) * mm});
            skLineSegment(sketch, "E1216", {"start": v(34.95, 20.17) * mm, "end": v(35.44, 20.84) * mm});
            skLineSegment(sketch, "E1217", {"start": v(35.44, 20.84) * mm, "end": v(35.73, 21.6) * mm});
            skLineSegment(sketch, "E1218", {"start": v(35.73, 21.6) * mm, "end": v(35.79, 22.37) * mm});
            skLineSegment(sketch, "E1219", {"start": v(35.79, 22.37) * mm, "end": v(35.76, 23.2) * mm});
            skLineSegment(sketch, "E1220", {"start": v(35.76, 23.2) * mm, "end": v(35.55, 23.85) * mm});
            skLineSegment(sketch, "E1221", {"start": v(35.55, 23.85) * mm, "end": v(34.89, 24.43) * mm});
            skLineSegment(sketch, "E1222", {"start": v(34.89, 24.43) * mm, "end": v(34.13, 24.74) * mm});
            skLineSegment(sketch, "E1223", {"start": v(34.13, 24.74) * mm, "end": v(33.49, 24.84) * mm});
            skLineSegment(sketch, "E1224", {"start": v(33.49, 24.84) * mm, "end": v(32.9, 24.7) * mm});
            skLineSegment(sketch, "E1225", {"start": v(32.9, 24.7) * mm, "end": v(32.6, 24.48) * mm});
            skLineSegment(sketch, "E1226", {"start": v(32.6, 24.48) * mm, "end": v(32.47, 24.13) * mm});
            skLineSegment(sketch, "E1227", {"start": v(32.47, 24.13) * mm, "end": v(32.57, 23.64) * mm});
            skLineSegment(sketch, "E1228", {"start": v(32.57, 23.64) * mm, "end": v(32.94, 23.37) * mm});
            skLineSegment(sketch, "E1229", {"start": v(32.94, 23.37) * mm, "end": v(33.28, 23.23) * mm});
            skLineSegment(sketch, "E1230", {"start": v(33.28, 23.23) * mm, "end": v(33.47, 23.08) * mm});
            skLineSegment(sketch, "E1231", {"start": v(33.47, 23.08) * mm, "end": v(33.21, 22.65) * mm});
            skLineSegment(sketch, "E1232", {"start": v(33.21, 22.65) * mm, "end": v(32.68, 22.49) * mm});
            skLineSegment(sketch, "E1233", {"start": v(32.68, 22.49) * mm, "end": v(32.23, 22.42) * mm});
            skLineSegment(sketch, "E1234", {"start": v(32.23, 22.42) * mm, "end": v(31, 23.02) * mm});
            skLineSegment(sketch, "E1235", {"start": v(31, 23.02) * mm, "end": v(30.58, 22.7) * mm});
            skLineSegment(sketch, "E1236", {"start": v(30.58, 22.7) * mm, "end": v(30.3, 22.21) * mm});
            skLineSegment(sketch, "E1237", {"start": v(30.3, 22.21) * mm, "end": v(30.03, 21.86) * mm});
            skLineSegment(sketch, "E1238", {"start": v(30.03, 21.86) * mm, "end": v(29.7, 21.57) * mm});
            skLineSegment(sketch, "E1239", {"start": v(29.7, 21.57) * mm, "end": v(29.22, 22.05) * mm});
            skLineSegment(sketch, "E1240", {"start": v(29.22, 22.05) * mm, "end": v(28.92, 22.53) * mm});
            skLineSegment(sketch, "E1241", {"start": v(28.92, 22.53) * mm, "end": v(29.05, 23.2) * mm});
            skLineSegment(sketch, "E1242", {"start": v(29.05, 23.2) * mm, "end": v(29.3, 23.72) * mm});
            skLineSegment(sketch, "E1243", {"start": v(29.3, 23.72) * mm, "end": v(29.51, 24.18) * mm});
            skLineSegment(sketch, "E1244", {"start": v(29.51, 24.18) * mm, "end": v(29.9, 24.43) * mm});
            skLineSegment(sketch, "E1245", {"start": v(29.9, 24.43) * mm, "end": v(29.14, 25.14) * mm});
            skLineSegment(sketch, "E1246", {"start": v(29.14, 25.14) * mm, "end": v(28.79, 25.6) * mm});
            skLineSegment(sketch, "E1247", {"start": v(28.79, 25.6) * mm, "end": v(28.72, 26.16) * mm});
            skLineSegment(sketch, "E1248", {"start": v(28.72, 26.16) * mm, "end": v(29.06, 26.43) * mm});
            skLineSegment(sketch, "E1249", {"start": v(29.06, 26.43) * mm, "end": v(29.29, 26.16) * mm});
            skLineSegment(sketch, "E1250", {"start": v(29.29, 26.16) * mm, "end": v(29.8, 25.82) * mm});
            skLineSegment(sketch, "E1251", {"start": v(29.8, 25.82) * mm, "end": v(30.27, 25.62) * mm});
            skLineSegment(sketch, "E1252", {"start": v(30.27, 25.62) * mm, "end": v(30.67, 25.62) * mm});
            skLineSegment(sketch, "E1253", {"start": v(30.67, 25.62) * mm, "end": v(31.2, 25.78) * mm});
            skLineSegment(sketch, "E1254", {"start": v(31.2, 25.78) * mm, "end": v(31.43, 26.06) * mm});
            skLineSegment(sketch, "E1255", {"start": v(31.43, 26.06) * mm, "end": v(31.69, 26.22) * mm});
            skLineSegment(sketch, "E1256", {"start": v(31.69, 26.22) * mm, "end": v(31.32, 27.1) * mm});
            skLineSegment(sketch, "E1257", {"start": v(31.32, 27.1) * mm, "end": v(31.4, 27.9) * mm});
            skLineSegment(sketch, "E1258", {"start": v(31.4, 27.9) * mm, "end": v(31.81, 28.65) * mm});
            skLineSegment(sketch, "E1259", {"start": v(31.81, 28.65) * mm, "end": v(32.3, 28.9) * mm});
            skLineSegment(sketch, "E1260", {"start": v(32.3, 28.9) * mm, "end": v(32.9, 29.04) * mm});
            skLineSegment(sketch, "E1261", {"start": v(32.9, 29.04) * mm, "end": v(32.75, 28.33) * mm});
            skLineSegment(sketch, "E1262", {"start": v(32.75, 28.33) * mm, "end": v(32.59, 27.81) * mm});
            skLineSegment(sketch, "E1263", {"start": v(32.59, 27.81) * mm, "end": v(32.72, 27.23) * mm});
            skLineSegment(sketch, "E1264", {"start": v(32.72, 27.23) * mm, "end": v(33.28, 26.81) * mm});
            skLineSegment(sketch, "E1265", {"start": v(33.28, 26.81) * mm, "end": v(34.07, 26.6) * mm});
            skLineSegment(sketch, "E1266", {"start": v(34.07, 26.6) * mm, "end": v(34.78, 26.27) * mm});
            skLineSegment(sketch, "E1267", {"start": v(34.78, 26.27) * mm, "end": v(35.42, 25.83) * mm});
            skLineSegment(sketch, "E1268", {"start": v(35.42, 25.83) * mm, "end": v(35.9, 25.48) * mm});
            skLineSegment(sketch, "E1269", {"start": v(35.9, 25.48) * mm, "end": v(35.89, 26.28) * mm});
            skLineSegment(sketch, "E1270", {"start": v(35.89, 26.28) * mm, "end": v(35.6, 27.22) * mm});
            skLineSegment(sketch, "E1271", {"start": v(35.6, 27.22) * mm, "end": v(35.07, 27.8) * mm});
            skLineSegment(sketch, "E1272", {"start": v(35.07, 27.8) * mm, "end": v(34.53, 28.47) * mm});
            skLineSegment(sketch, "E1273", {"start": v(34.53, 28.47) * mm, "end": v(33.9, 29.25) * mm});
            skLineSegment(sketch, "E1274", {"start": v(33.9, 29.25) * mm, "end": v(33.25, 29.9) * mm});
            skLineSegment(sketch, "E1275", {"start": v(33.25, 29.9) * mm, "end": v(32.44, 30.55) * mm});
            skLineSegment(sketch, "E1276", {"start": v(32.44, 30.55) * mm, "end": v(31.51, 31.36) * mm});
            skLineSegment(sketch, "E1277", {"start": v(31.51, 31.36) * mm, "end": v(30.6, 32.31) * mm});
            skLineSegment(sketch, "E1278", {"start": v(30.6, 32.31) * mm, "end": v(29.95, 33.52) * mm});
            skLineSegment(sketch, "E1279", {"start": v(29.95, 33.52) * mm, "end": v(29.45, 34.53) * mm});
            skLineSegment(sketch, "E1280", {"start": v(29.45, 34.53) * mm, "end": v(29.18, 35.74) * mm});
            skLineSegment(sketch, "E1281", {"start": v(29.18, 35.74) * mm, "end": v(29.1, 36.87) * mm});
            skLineSegment(sketch, "E1282", {"start": v(29.1, 36.87) * mm, "end": v(29.04, 37.73) * mm});
            skLineSegment(sketch, "E1283", {"start": v(29.04, 37.73) * mm, "end": v(29.21, 38.74) * mm});
            skLineSegment(sketch, "E1284", {"start": v(29.21, 38.74) * mm, "end": v(29.44, 39.7) * mm});
            skLineSegment(sketch, "E1285", {"start": v(29.44, 39.7) * mm, "end": v(29.66, 40.39) * mm});
            skLineSegment(sketch, "E1286", {"start": v(29.66, 40.39) * mm, "end": v(30.04, 41.06) * mm});
            skLineSegment(sketch, "E1287", {"start": v(30.04, 41.06) * mm, "end": v(30.59, 41.67) * mm});
            skLineSegment(sketch, "E1288", {"start": v(30.59, 41.67) * mm, "end": v(31.23, 42.22) * mm});
            skLineSegment(sketch, "E1289", {"start": v(31.23, 42.22) * mm, "end": v(31.87, 42.56) * mm});
            skLineSegment(sketch, "E1290", {"start": v(31.87, 42.56) * mm, "end": v(32.55, 42.81) * mm});
            skLineSegment(sketch, "E1291", {"start": v(32.55, 42.81) * mm, "end": v(33.32, 43) * mm});
            skLineSegment(sketch, "E1292", {"start": v(33.32, 43) * mm, "end": v(34.07, 43.06) * mm});
            skLineSegment(sketch, "E1293", {"start": v(34.07, 43.06) * mm, "end": v(34.55, 43.12) * mm});
            skLineSegment(sketch, "E1294", {"start": v(34.55, 43.12) * mm, "end": v(34.86, 43.3) * mm});
            skLineSegment(sketch, "E1295", {"start": v(34.86, 43.3) * mm, "end": v(35.32, 43.7) * mm});
            skLineSegment(sketch, "E1296", {"start": v(35.32, 43.7) * mm, "end": v(35.6, 44.13) * mm});
            skLineSegment(sketch, "E1297", {"start": v(35.6, 44.13) * mm, "end": v(35.9, 44.6) * mm});
            skLineSegment(sketch, "E1298", {"start": v(35.9, 44.6) * mm, "end": v(36.11, 44.47) * mm});
            skLineSegment(sketch, "E1299", {"start": v(36.11, 44.47) * mm, "end": v(36.4, 44.12) * mm});
            skLineSegment(sketch, "E1300", {"start": v(36.4, 44.12) * mm, "end": v(36.5, 43.7) * mm});
            skLineSegment(sketch, "E1301", {"start": v(36.5, 43.7) * mm, "end": v(36.45, 43.27) * mm});
            skLineSegment(sketch, "E1302", {"start": v(36.45, 43.27) * mm, "end": v(36.27, 42.7) * mm});
            skLineSegment(sketch, "E1303", {"start": v(36.27, 42.7) * mm, "end": v(36.09, 42.45) * mm});
            skLineSegment(sketch, "E1304", {"start": v(36.09, 42.45) * mm, "end": v(36.56, 42.15) * mm});
            skLineSegment(sketch, "E1305", {"start": v(36.56, 42.15) * mm, "end": v(36.94, 41.77) * mm});
            skLineSegment(sketch, "E1306", {"start": v(36.94, 41.77) * mm, "end": v(37.21, 41.4) * mm});
            skLineSegment(sketch, "E1307", {"start": v(37.21, 41.4) * mm, "end": v(37.46, 41) * mm});
            skLineSegment(sketch, "E1308", {"start": v(37.46, 41) * mm, "end": v(37.64, 40.69) * mm});
            skLineSegment(sketch, "E1309", {"start": v(37.64, 40.69) * mm, "end": v(37.78, 40.37) * mm});
            skLineSegment(sketch, "E1310", {"start": v(37.78, 40.37) * mm, "end": v(38.1, 40.37) * mm});
            skLineSegment(sketch, "E1311", {"start": v(38.1, 40.37) * mm, "end": v(38.63, 40.4) * mm});
            skLineSegment(sketch, "E1312", {"start": v(38.63, 40.4) * mm, "end": v(39.1, 40.55) * mm});
            skLineSegment(sketch, "E1313", {"start": v(39.1, 40.55) * mm, "end": v(39.52, 40.73) * mm});
            skLineSegment(sketch, "E1314", {"start": v(39.52, 40.73) * mm, "end": v(39.73, 40.84) * mm});
            skLineSegment(sketch, "E1315", {"start": v(39.73, 40.84) * mm, "end": v(39.94, 40.6) * mm});
            skLineSegment(sketch, "E1316", {"start": v(39.94, 40.6) * mm, "end": v(39.82, 39.88) * mm});
            skLineSegment(sketch, "E1317", {"start": v(39.82, 39.88) * mm, "end": v(39.57, 39.55) * mm});
            skLineSegment(sketch, "E1318", {"start": v(39.57, 39.55) * mm, "end": v(39.17, 39.18) * mm});
            skLineSegment(sketch, "E1319", {"start": v(39.17, 39.18) * mm, "end": v(38.8, 38.97) * mm});
            skLineSegment(sketch, "E1320", {"start": v(38.8, 38.97) * mm, "end": v(38.65, 38.7) * mm});
            skLineSegment(sketch, "E1321", {"start": v(38.65, 38.7) * mm, "end": v(38.56, 38.35) * mm});
            skLineSegment(sketch, "E1322", {"start": v(38.56, 38.35) * mm, "end": v(38.48, 37.92) * mm});
            skLineSegment(sketch, "E1323", {"start": v(38.48, 37.92) * mm, "end": v(38.49, 37.48) * mm});
            skLineSegment(sketch, "E1324", {"start": v(38.49, 37.48) * mm, "end": v(38.55, 37.24) * mm});
            skLineSegment(sketch, "E1325", {"start": v(38.55, 37.24) * mm, "end": v(38.77, 36.63) * mm});
            skLineSegment(sketch, "E1326", {"start": v(38.77, 36.63) * mm, "end": v(39.02, 36.3) * mm});
            skLineSegment(sketch, "E1327", {"start": v(39.02, 36.3) * mm, "end": v(39.24, 36) * mm});
            skLineSegment(sketch, "E1328", {"start": v(39.24, 36) * mm, "end": v(39.01, 35.8) * mm});
            skLineSegment(sketch, "E1329", {"start": v(39.01, 35.8) * mm, "end": v(38.53, 35.74) * mm});
            skLineSegment(sketch, "E1330", {"start": v(38.53, 35.74) * mm, "end": v(37.93, 35.87) * mm});
            skLineSegment(sketch, "E1331", {"start": v(37.93, 35.87) * mm, "end": v(37.42, 36.18) * mm});
            skLineSegment(sketch, "E1332", {"start": v(37.42, 36.18) * mm, "end": v(37.13, 36.44) * mm});
            skLineSegment(sketch, "E1333", {"start": v(37.13, 36.44) * mm, "end": v(36.93, 36.67) * mm});
            skLineSegment(sketch, "E1334", {"start": v(36.93, 36.67) * mm, "end": v(36.76, 36.23) * mm});
            skLineSegment(sketch, "E1335", {"start": v(36.76, 36.23) * mm, "end": v(36.52, 35.72) * mm});
            skLineSegment(sketch, "E1336", {"start": v(36.52, 35.72) * mm, "end": v(36.4, 35.3) * mm});
            skLineSegment(sketch, "E1337", {"start": v(36.4, 35.3) * mm, "end": v(36.3, 34.96) * mm});
            skLineSegment(sketch, "E1338", {"start": v(36.3, 34.96) * mm, "end": v(36.36, 34.6) * mm});
            skLineSegment(sketch, "E1339", {"start": v(36.36, 34.6) * mm, "end": v(36.4, 34.29) * mm});
            skLineSegment(sketch, "E1340", {"start": v(36.4, 34.29) * mm, "end": v(36.56, 34.04) * mm});
            skLineSegment(sketch, "E1341", {"start": v(36.56, 34.04) * mm, "end": v(36.28, 33.96) * mm});
            skLineSegment(sketch, "E1342", {"start": v(36.28, 33.96) * mm, "end": v(34.84, 34.53) * mm});
            skLineSegment(sketch, "E1343", {"start": v(34.84, 34.53) * mm, "end": v(34.27, 35.05) * mm});
            skLineSegment(sketch, "E1344", {"start": v(34.27, 35.05) * mm, "end": v(33.75, 35.62) * mm});
            skLineSegment(sketch, "E1345", {"start": v(33.75, 35.62) * mm, "end": v(33.64, 36.35) * mm});
            skLineSegment(sketch, "E1346", {"start": v(33.64, 36.35) * mm, "end": v(33.73, 36.99) * mm});
            skLineSegment(sketch, "E1347", {"start": v(33.73, 36.99) * mm, "end": v(34, 37.42) * mm});
            skLineSegment(sketch, "E1348", {"start": v(34, 37.42) * mm, "end": v(33.98, 37.87) * mm});
            skLineSegment(sketch, "E1349", {"start": v(33.98, 37.87) * mm, "end": v(33.81, 37.75) * mm});
            skLineSegment(sketch, "E1350", {"start": v(33.81, 37.75) * mm, "end": v(33.42, 37.77) * mm});
            skLineSegment(sketch, "E1351", {"start": v(33.42, 37.77) * mm, "end": v(33.34, 38.09) * mm});
            skLineSegment(sketch, "E1352", {"start": v(33.34, 38.09) * mm, "end": v(33.48, 38.7) * mm});
            skLineSegment(sketch, "E1353", {"start": v(33.48, 38.7) * mm, "end": v(33.65, 39.76) * mm});
            skLineSegment(sketch, "E1354", {"start": v(33.65, 39.76) * mm, "end": v(33.78, 40.64) * mm});
            skLineSegment(sketch, "E1355", {"start": v(33.78, 40.64) * mm, "end": v(33.91, 41.18) * mm});
            skLineSegment(sketch, "E1356", {"start": v(33.91, 41.18) * mm, "end": v(33.86, 41.5) * mm});
            skLineSegment(sketch, "E1357", {"start": v(33.86, 41.5) * mm, "end": v(32.6, 41.38) * mm});
            skLineSegment(sketch, "E1358", {"start": v(32.6, 41.38) * mm, "end": v(31.78, 41) * mm});
            skLineSegment(sketch, "E1359", {"start": v(31.78, 41) * mm, "end": v(31.22, 40.27) * mm});
            skLineSegment(sketch, "E1360", {"start": v(31.22, 40.27) * mm, "end": v(30.82, 39.47) * mm});
            skLineSegment(sketch, "E1361", {"start": v(30.82, 39.47) * mm, "end": v(30.5, 38.66) * mm});
            skLineSegment(sketch, "E1362", {"start": v(30.5, 38.66) * mm, "end": v(30.4, 37.91) * mm});
            skLineSegment(sketch, "E1363", {"start": v(30.4, 37.91) * mm, "end": v(30.32, 36.64) * mm});
            skLineSegment(sketch, "E1364", {"start": v(30.32, 36.64) * mm, "end": v(30.62, 35.52) * mm});
            skLineSegment(sketch, "E1365", {"start": v(30.62, 35.52) * mm, "end": v(31, 34.54) * mm});
            skLineSegment(sketch, "E1366", {"start": v(31, 34.54) * mm, "end": v(31.52, 33.7) * mm});
            skLineSegment(sketch, "E1367", {"start": v(31.52, 33.7) * mm, "end": v(32.05, 33.03) * mm});
            skLineSegment(sketch, "E1368", {"start": v(32.05, 33.03) * mm, "end": v(32.73, 32.41) * mm});
            skLineSegment(sketch, "E1369", {"start": v(32.73, 32.41) * mm, "end": v(33.38, 31.89) * mm});
            skLineSegment(sketch, "E1370", {"start": v(33.38, 31.89) * mm, "end": v(34.12, 31.13) * mm});
            skLineSegment(sketch, "E1371", {"start": v(34.12, 31.13) * mm, "end": v(34.82, 30.46) * mm});
            skLineSegment(sketch, "E1372", {"start": v(34.82, 30.46) * mm, "end": v(35.53, 29.83) * mm});
            skLineSegment(sketch, "E1373", {"start": v(35.53, 29.83) * mm, "end": v(36.5, 28.5) * mm});
            skLineSegment(sketch, "E1374", {"start": v(36.5, 28.5) * mm, "end": v(37.28, 26.8) * mm});
            skLineSegment(sketch, "E1375", {"start": v(37.28, 26.8) * mm, "end": v(37.61, 25.77) * mm});
            skLineSegment(sketch, "E1376", {"start": v(37.61, 25.77) * mm, "end": v(37.82, 24.63) * mm});
            skLineSegment(sketch, "E1377", {"start": v(37.82, 24.63) * mm, "end": v(38, 23.32) * mm});
            skLineSegment(sketch, "E1378", {"start": v(38, 23.32) * mm, "end": v(37.93, 22.05) * mm});
            skLineSegment(sketch, "E1379", {"start": v(37.93, 22.05) * mm, "end": v(37.58, 20.73) * mm});
            skLineSegment(sketch, "E1380", {"start": v(37.58, 20.73) * mm, "end": v(36.95, 19.6) * mm});
            skLineSegment(sketch, "E1381", {"start": v(36.95, 19.6) * mm, "end": v(36.1, 18.63) * mm});
            skLineSegment(sketch, "E1382", {"start": v(36.1, 18.63) * mm, "end": v(34.88, 17.7) * mm});
            skLineSegment(sketch, "E1383", {"start": v(34.88, 17.7) * mm, "end": v(33.67, 17.37) * mm});
            skLineSegment(sketch, "E1384", {"start": v(33.67, 17.37) * mm, "end": v(32.6, 17.24) * mm});
            skLineSegment(sketch, "E1385", {"start": v(32.6, 17.24) * mm, "end": v(31.29, 17.29) * mm});
            skLineSegment(sketch, "E1386", {"start": v(31.29, 17.29) * mm, "end": v(29.85, 17.42) * mm});
            skLineSegment(sketch, "E1387", {"start": v(29.85, 17.42) * mm, "end": v(28.34, 17.71) * mm});
            skSolve(sketch);
        }
        {
            var Q0;
            Q0=makeQuery(id+"F0.imprint","IMPRINT",FACE,{"disambiguationData":[TD([[makeQuery(id+"F0.imprint","IMPRINT",EDGE,{"derivedFrom":sQuery(id+"F0.wireOp",EDGE,"E0")}),-1.0]])]});
            extrude(context, id + "F1", {"entities" : qUnion([Q0]), "depth" : 2 * mm, "offsetDistance" : 25 * mm});
        }
        {
            var Q0;
            Q0=qCreatedBy(makeId("Top.planeOp"),FACE);
            var sketch = newSketch(context, id + "F2", { "sketchPlane" : qUnion([Q0])});
            skText(sketch, "E1388", { "text": "TRACEY", "fontName": "OpenSans-Bold.ttf"});
            const initialGuessF2  = {"E1388": [-4e-05, -0.00933, 1, 0, 0.0075]};
            skSetInitialGuess(sketch, initialGuessF2);
            skSolve(sketch);
        }
        {
            var Q0;
            Q0=makeQuery(id+"F2.imprint","IMPRINT",FACE,{"disambiguationData":[TD([[makeQuery(id+"F2.imprint","IMPRINT",EDGE,{"derivedFrom":sQuery(id+"F2.wireOp",EDGE,"E1388.sketch_text.stroke-0")}),-1.0]])]});
            var Q1;
            Q1=makeQuery(id+"F2.imprint","IMPRINT",FACE,{"disambiguationData":[TD([[makeQuery(id+"F2.imprint","IMPRINT",EDGE,{"derivedFrom":sQuery(id+"F2.wireOp",EDGE,"E1388.sketch_text.stroke-8")}),-1.0]])]});
            var Q2;
            Q2=makeQuery(id+"F2.imprint","IMPRINT",FACE,{"disambiguationData":[TD([[makeQuery(id+"F2.imprint","IMPRINT",EDGE,{"derivedFrom":sQuery(id+"F2.wireOp",EDGE,"E1388.sketch_text.stroke-27")}),-1.0]])]});
            var Q3;
            Q3=makeQuery(id+"F2.imprint","IMPRINT",FACE,{"disambiguationData":[TD([[makeQuery(id+"F2.imprint","IMPRINT",EDGE,{"derivedFrom":sQuery(id+"F2.wireOp",EDGE,"E1388.sketch_text.stroke-39")}),-1.0]])]});
            var Q4;
            Q4=makeQuery(id+"F2.imprint","IMPRINT",FACE,{"disambiguationData":[TD([[makeQuery(id+"F2.imprint","IMPRINT",EDGE,{"derivedFrom":sQuery(id+"F2.wireOp",EDGE,"E1388.sketch_text.stroke-54")}),-1.0]])]});
            var Q5;
            Q5=makeQuery(id+"F2.imprint","IMPRINT",FACE,{"disambiguationData":[TD([[makeQuery(id+"F2.imprint","IMPRINT",EDGE,{"derivedFrom":sQuery(id+"F2.wireOp",EDGE,"E1388.sketch_text.stroke-66")}),-1.0]])]});
            extrude(context, id + "F3", {"entities" : qUnion([Q0, Q1, Q2, Q3, Q4, Q5]), "depth" : 2 * mm, "offsetDistance" : 25 * mm});
        }
    });
